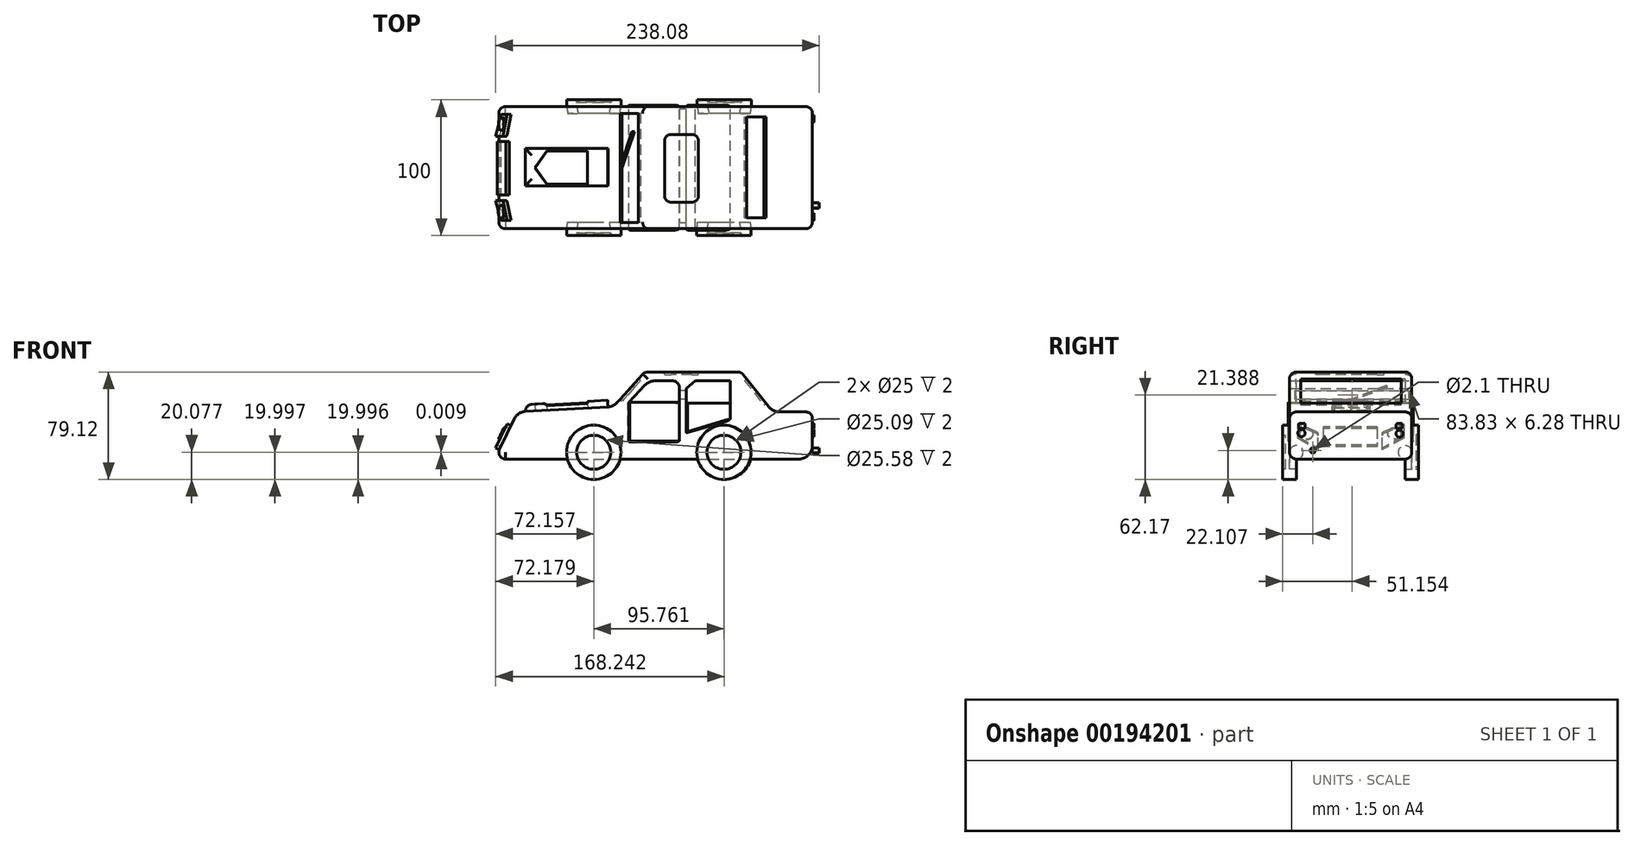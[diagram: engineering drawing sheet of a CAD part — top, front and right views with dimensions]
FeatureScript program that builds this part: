
annotation { "Feature Type Name" : "Feature", "Feature Type Description" : "" }
export const myFeature = defineFeature(function(context is Context, id is Id, definition is map)
    precondition{}
    {
        {
            var Q0;
            Q0=qCreatedBy(makeId("Front.planeOp"),FACE);
            var sketch = newSketch(context, id + "F0", { "sketchPlane" : qUnion([Q0])});
            skLineSegment(sketch, "E0.right", {"start": v(123.47, 0) * mm, "end": v(123.47, -24.73) * mm});
            skLineSegment(sketch, "E1", {"start": v(-110.25, -34.75) * mm, "end": v(-96.18, -5.34) * mm});
            skLineSegment(sketch, "E2", {"start": v(-87.7, 0.33) * mm, "end": v(-26.96, 3.68) * mm});
            skLineSegment(sketch, "E3", {"start": v(-20.07, 6.99) * mm, "end": v(0, 29.38) * mm});
            skLineSegment(sketch, "E4", {"start": v(0, 29.38) * mm, "end": v(70.99, 29.38) * mm});
            skLineSegment(sketch, "E5", {"start": v(70.99, 29.38) * mm, "end": v(91.24, 3.8) * mm});
            skLineSegment(sketch, "E6", {"start": v(99.08, 0) * mm, "end": v(123.47, 0) * mm});
            skLineSegment(sketch, "E7", {"start": v(-110.25, -34.75) * mm, "end": v(-48.86, -34.74) * mm});
            skLineSegment(sketch, "E8.trimOffspring", {"start": v(-8.86, -34.74) * mm, "end": v(46.53, -34.73) * mm});
            skLineSegment(sketch, "E9.trimOffspring", {"start": v(86.53, -34.73) * mm, "end": v(113.47, -34.73) * mm});
            skPoint(sketch, "E10.visualSharp", {"position": v(-22.83, 3.9) * mm});
            skArc(sketch, "E10.filletArc", {"start": v(-26.96, 3.68) * mm, "mid": v(-23.19, 4.65) * mm, "end": v(-20.07, 6.99) * mm});
            skPoint(sketch, "E11.visualSharp", {"position": v(94.24, 0) * mm});
            skArc(sketch, "E11.filletArc", {"start": v(91.24, 3.8) * mm, "mid": v(94.72, 1) * mm, "end": v(99.08, 0) * mm});
            skPoint(sketch, "E12.visualSharp", {"position": v(-93.62, 0) * mm});
            skArc(sketch, "E12.filletArc", {"start": v(-87.7, 0.33) * mm, "mid": v(-92.72, -1.35) * mm, "end": v(-96.18, -5.34) * mm});
            skPoint(sketch, "E13.visualSharp", {"position": v(123.47, -34.73) * mm});
            skArc(sketch, "E13.filletArc", {"start": v(113.47, -34.73) * mm, "mid": v(120.54, -31.8) * mm, "end": v(123.47, -24.73) * mm});
            skLineSegment(sketch, "E14", {"start": v(-11.64, 6.99) * mm, "end": v(0.27, 19.72) * mm});
            skLineSegment(sketch, "E15", {"start": v(7.57, 22.88) * mm, "end": v(20.47, 22.88) * mm});
            skLineSegment(sketch, "E16", {"start": v(25.47, 17.88) * mm, "end": v(25.47, 6.99) * mm});
            skLineSegment(sketch, "E17", {"start": v(25.47, 6.99) * mm, "end": v(-11.64, 6.99) * mm});
            skPoint(sketch, "E18.visualSharp", {"position": v(3.24, 22.88) * mm});
            skArc(sketch, "E18.filletArc", {"start": v(7.57, 22.88) * mm, "mid": v(3.6, 22.06) * mm, "end": v(0.27, 19.72) * mm});
            skPoint(sketch, "E19.visualSharp", {"position": v(25.47, 22.88) * mm});
            skArc(sketch, "E19.filletArc", {"start": v(25.47, 17.88) * mm, "mid": v(24, 21.42) * mm, "end": v(20.47, 22.88) * mm});
            skLineSegment(sketch, "E20", {"start": v(30.75, 17.27) * mm, "end": v(30.75, 6.6) * mm});
            skLineSegment(sketch, "E21", {"start": v(30.75, 6.6) * mm, "end": v(63.04, 6.6) * mm});
            skLineSegment(sketch, "E22", {"start": v(63.04, 6.6) * mm, "end": v(63.04, 22.88) * mm});
            skLineSegment(sketch, "E23", {"start": v(63.04, 22.88) * mm, "end": v(37.2, 22.88) * mm});
            skLineSegment(sketch, "E24", {"start": v(37.2, 22.88) * mm, "end": v(30.75, 17.27) * mm});
            skLineSegment(sketch, "E25", {"start": v(-48.86, -34.74) * mm, "end": v(-8.86, -34.74) * mm});
            skLineSegment(sketch, "E26", {"start": v(46.53, -34.73) * mm, "end": v(86.53, -34.73) * mm});
            skSolve(sketch);
        }
        {
            var Q0;
            Q0=makeQuery(id+"F0.imprint","IMPRINT",FACE,{"disambiguationData":[TD([[makeQuery(id+"F0.imprint","IMPRINT",EDGE,{"derivedFrom":sQuery(id+"F0.wireOp",EDGE,"E1")}),-1.0]])]});
            extrude(context, id + "F1", {"entities" : qUnion([Q0]), "endBound" : BoundingType.SYMMETRIC, "depth" : 90 * mm});
        }
        {
            var Q0;
            Q0=makeQuery(id+"F1.opExtrude","CAP_EDGE",EDGE,{"disambiguationData":[OSD([sQuery(id+"F0.wireOp",EDGE,"E8.trimOffspring")])],"isStart":false});
            var Q1;
            Q1=makeQuery(id+"F1.opExtrude","CAP_EDGE",EDGE,{"disambiguationData":[OSD([sQuery(id+"F0.wireOp",EDGE,"E9.trimOffspring")])],"isStart":false});
            var Q2;
            Q2=makeQuery(id+"F1.opExtrude","CAP_EDGE",EDGE,{"disambiguationData":[OSD([sQuery(id+"F0.wireOp",EDGE,"E7")])],"isStart":false});
            var Q3;
            Q3=makeQuery(id+"F1.opExtrude","CAP_EDGE",EDGE,{"disambiguationData":[OSD([sQuery(id+"F0.wireOp",EDGE,"E7")])],"isStart":true});
            var Q4;
            Q4=makeQuery(id+"F1.opExtrude","CAP_EDGE",EDGE,{"disambiguationData":[OSD([sQuery(id+"F0.wireOp",EDGE,"E8.trimOffspring")])],"isStart":true});
            var Q5;
            Q5=makeQuery(id+"F1.opExtrude","CAP_EDGE",EDGE,{"disambiguationData":[OSD([sQuery(id+"F0.wireOp",EDGE,"E9.trimOffspring")])],"isStart":true});
            fillet(context, id + "F2", {"entities" : qUnion([Q0, Q1, Q2, Q3, Q4, Q5]), "radius" : 5 * mm, "tangentPropagation" : true, "allowEdgeOverflow" : false});
        }
        {
            var Q0;
            Q0=makeQuery(id+"F1.opExtrude","CAP_EDGE",EDGE,{"disambiguationData":[OSD([sQuery(id+"F0.wireOp",EDGE,"E5")])],"isStart":false});
            var Q1;
            Q1=makeQuery(id+"F1.opExtrude","CAP_EDGE",EDGE,{"disambiguationData":[OSD([sQuery(id+"F0.wireOp",EDGE,"E4")])],"isStart":false});
            var Q2;
            Q2=makeQuery(id+"F1.opExtrude","SWEPT_EDGE",EDGE,{"disambiguationData":[OSD([sQuery(id+"F0.wireOp",EDGE,"E4"),sQuery(id+"F0.wireOp",EDGE,"E5")])]});
            var Q3;
            Q3=makeQuery(id+"F1.opExtrude","CAP_EDGE",EDGE,{"disambiguationData":[OSD([sQuery(id+"F0.wireOp",EDGE,"E4")])],"isStart":true});
            var Q4;
            Q4=makeQuery(id+"F1.opExtrude","SWEPT_EDGE",EDGE,{"disambiguationData":[OSD([sQuery(id+"F0.wireOp",EDGE,"E3"),sQuery(id+"F0.wireOp",EDGE,"E4")])]});
            fillet(context, id + "F3", {"entities" : qUnion([Q0, Q1, Q2, Q3, Q4]), "radius" : 5 * mm, "tangentPropagation" : true, "allowEdgeOverflow" : false});
        }
        {
            var Q0;
            Q0=makeQuery(id+"F1.opExtrude","SWEPT_FACE",FACE,{"disambiguationData":[OSD([sQuery(id+"F0.wireOp",EDGE,"E1")])]});
            var sketch = newSketch(context, id + "F4", { "sketchPlane" : qUnion([Q0])});
            skLineSegment(sketch, "E27", {"start": v(-39.13, -51.46) * mm, "end": v(-39.13, -60.89) * mm});
            skLineSegment(sketch, "E28", {"start": v(-38.12, -62.62) * mm, "end": v(-23.15, -71.18) * mm});
            skLineSegment(sketch, "E29", {"start": v(-23.15, -71.18) * mm, "end": v(-23.15, -59.81) * mm});
            skLineSegment(sketch, "E30", {"start": v(-24.34, -57.98) * mm, "end": v(-39.13, -51.46) * mm});
            skLineSegment(sketch, "E31", {"start": v(38.83, -51.46) * mm, "end": v(38.83, -60.94) * mm});
            skLineSegment(sketch, "E32", {"start": v(37.89, -62.63) * mm, "end": v(24.19, -71.18) * mm});
            skLineSegment(sketch, "E33", {"start": v(24.19, -71.18) * mm, "end": v(24.19, -59.76) * mm});
            skLineSegment(sketch, "E34", {"start": v(25.32, -57.96) * mm, "end": v(38.83, -51.46) * mm});
            skPoint(sketch, "E35.visualSharp", {"position": v(-23.15, -58.5) * mm});
            skArc(sketch, "E35.filletArc", {"start": v(-23.15, -59.81) * mm, "mid": v(-23.47, -58.72) * mm, "end": v(-24.34, -57.98) * mm});
            skPoint(sketch, "E36.visualSharp", {"position": v(-39.13, -62.05) * mm});
            skArc(sketch, "E36.filletArc", {"start": v(-39.13, -60.89) * mm, "mid": v(-38.86, -61.9) * mm, "end": v(-38.12, -62.62) * mm});
            skPoint(sketch, "E37.visualSharp", {"position": v(24.19, -58.5) * mm});
            skArc(sketch, "E37.filletArc", {"start": v(25.32, -57.96) * mm, "mid": v(24.5, -58.7) * mm, "end": v(24.19, -59.76) * mm});
            skPoint(sketch, "E38.visualSharp", {"position": v(38.83, -62.05) * mm});
            skArc(sketch, "E38.filletArc", {"start": v(37.89, -62.63) * mm, "mid": v(38.58, -61.9) * mm, "end": v(38.83, -60.94) * mm});
            skCircle(sketch, "E39", {"center": v(-32.1, -59.81) * mm, "radius": 4.75 * mm});
            skCircle(sketch, "E40", {"center": v(32.5, -59.99) * mm, "radius": 4.75 * mm});
            skPoint(sketch, "E41.oppositeSnap0", {"position": v(40, -67.86) * mm});
            skLineSegment(sketch, "E41.bottom", {"start": v(-39.86, -48.02) * mm, "end": v(40, -48.02) * mm});
            skLineSegment(sketch, "E41.top", {"start": v(-39.86, -71.3) * mm, "end": v(40, -71.3) * mm});
            skLineSegment(sketch, "E41.left", {"start": v(-39.86, -48.02) * mm, "end": v(-39.86, -71.3) * mm});
            skLineSegment(sketch, "E41.right", {"start": v(40, -48.02) * mm, "end": v(40, -71.3) * mm});
            skLineSegment(sketch, "E42.bottom", {"start": v(-19.4, -54) * mm, "end": v(20.24, -54) * mm});
            skLineSegment(sketch, "E42.top", {"start": v(-19.4, -68.74) * mm, "end": v(20.24, -68.74) * mm});
            skLineSegment(sketch, "E42.left", {"start": v(-19.4, -54) * mm, "end": v(-19.4, -68.74) * mm});
            skLineSegment(sketch, "E42.right", {"start": v(20.24, -54) * mm, "end": v(20.24, -68.74) * mm});
            skSolve(sketch);
        }
        {
            var Q0;
            Q0=makeQuery(id+"F4.imprint","IMPRINT",FACE,{"disambiguationData":[TD([[makeQuery(id+"F4.imprint","IMPRINT",EDGE,{"derivedFrom":sQuery(id+"F4.wireOp",EDGE,"E27")}),-1.0]])]});
            extrude(context, id + "F5", {"entities" : qUnion([Q0]), "operationType" : NewBodyOperationType.REMOVE, "depth" : 2 * mm});
        }
        {
            var Q0;
            Q0=makeQuery(id+"F1.opExtrude","SWEPT_FACE",FACE,{"disambiguationData":[OSD([sQuery(id+"F0.wireOp",EDGE,"E3")])]});
            var sketch = newSketch(context, id + "F6", { "sketchPlane" : qUnion([Q0])});
            skLineSegment(sketch, "E43.bottom", {"start": v(-40, 15.17) * mm, "end": v(40.3, 15.17) * mm});
            skLineSegment(sketch, "E43.top", {"start": v(-40, -5.22) * mm, "end": v(40.3, -5.22) * mm});
            skLineSegment(sketch, "E43.left", {"start": v(-40, 15.17) * mm, "end": v(-40, -5.22) * mm});
            skLineSegment(sketch, "E43.right", {"start": v(40.3, 15.17) * mm, "end": v(40.3, -5.22) * mm});
            skLineSegment(sketch, "E44", {"start": v(-26.5, 8.65) * mm, "end": v(0, -5.22) * mm});
            skLineSegment(sketch, "E45", {"start": v(-26.64, 7.88) * mm, "end": v(-0.65, -4.88) * mm});
            skLineSegment(sketch, "E46", {"start": v(-26.5, 8.65) * mm, "end": v(-26.64, 7.88) * mm});
            skSolve(sketch);
        }
        {
            var Q0;
            Q0=makeQuery(id+"F6.imprint","IMPRINT",FACE,{"disambiguationData":[TD([[makeQuery(id+"F6.imprint","IMPRINT",EDGE,{"derivedFrom":sQuery(id+"F6.wireOp",EDGE,"E43.bottom")}),-1.0]])]});
            extrude(context, id + "F7", {"entities" : qUnion([Q0]), "operationType" : NewBodyOperationType.REMOVE, "oppositeDirection" : true, "depth" : 2 * mm});
        }
        {
            var Q0;
            Q0=makeQuery(id+"F1.opExtrude","SWEPT_FACE",FACE,{"disambiguationData":[OSD([sQuery(id+"F0.wireOp",EDGE,"E5")])]});
            var sketch = newSketch(context, id + "F8", { "sketchPlane" : qUnion([Q0])});
            skLineSegment(sketch, "E47.bottom", {"start": v(-36.85, -27.57) * mm, "end": v(37.38, -27.57) * mm});
            skLineSegment(sketch, "E47.top", {"start": v(-36.85, -50.4) * mm, "end": v(37.38, -50.4) * mm});
            skLineSegment(sketch, "E47.left", {"start": v(-36.85, -27.57) * mm, "end": v(-36.85, -50.4) * mm});
            skLineSegment(sketch, "E47.right", {"start": v(37.38, -27.57) * mm, "end": v(37.38, -50.4) * mm});
            skSolve(sketch);
        }
        {
            var Q0;
            Q0=makeQuery(id+"F8.imprint","IMPRINT",FACE,{"disambiguationData":[TD([[makeQuery(id+"F8.imprint","IMPRINT",EDGE,{"derivedFrom":sQuery(id+"F8.wireOp",EDGE,"E47.bottom")}),-1.0]])]});
            extrude(context, id + "F9", {"entities" : qUnion([Q0]), "operationType" : NewBodyOperationType.REMOVE, "oppositeDirection" : true, "depth" : 2 * mm});
        }
        {
            var Q0;
            Q0=makeQuery(id+"F1.opExtrude","SWEPT_FACE",FACE,{"disambiguationData":[OSD([sQuery(id+"F0.wireOp",EDGE,"E0.right")])]});
            var sketch = newSketch(context, id + "F10", { "sketchPlane" : qUnion([Q0])});
            skLineSegment(sketch, "E48.bottom", {"start": v(-37.41, -8.5) * mm, "end": v(-33.54, -8.5) * mm});
            skLineSegment(sketch, "E48.top", {"start": v(-38.45, -12.4) * mm, "end": v(-34.58, -12.4) * mm});
            skLineSegment(sketch, "E48.left", {"start": v(-38.45, -9.54) * mm, "end": v(-38.45, -12.4) * mm});
            skLineSegment(sketch, "E48.right", {"start": v(-33.54, -8.5) * mm, "end": v(-33.54, -11.36) * mm});
            skLineSegment(sketch, "E49.bottom", {"start": v(34.53, -8.5) * mm, "end": v(38.02, -8.5) * mm});
            skLineSegment(sketch, "E49.top", {"start": v(33.49, -12.4) * mm, "end": v(36.98, -12.4) * mm});
            skLineSegment(sketch, "E49.left", {"start": v(33.49, -9.55) * mm, "end": v(33.49, -12.4) * mm});
            skLineSegment(sketch, "E49.right", {"start": v(38.02, -8.5) * mm, "end": v(38.02, -11.36) * mm});
            skCircle(sketch, "E50", {"center": v(-36.21, -15.58) * mm, "radius": 2.68 * mm});
            skCircle(sketch, "E51", {"center": v(35.98, -16.04) * mm, "radius": 2.6 * mm});
            skPoint(sketch, "E52.visualSharp", {"position": v(-38.45, -8.5) * mm});
            skArc(sketch, "E52.filletArc", {"start": v(-37.41, -8.5) * mm, "mid": v(-38.15, -8.81) * mm, "end": v(-38.45, -9.54) * mm});
            skPoint(sketch, "E53.visualSharp", {"position": v(-33.54, -12.4) * mm});
            skArc(sketch, "E53.filletArc", {"start": v(-34.58, -12.4) * mm, "mid": v(-33.84, -12.1) * mm, "end": v(-33.54, -11.36) * mm});
            skPoint(sketch, "E54.visualSharp", {"position": v(33.49, -8.5) * mm});
            skArc(sketch, "E54.filletArc", {"start": v(34.53, -8.5) * mm, "mid": v(33.8, -8.81) * mm, "end": v(33.49, -9.55) * mm});
            skPoint(sketch, "E55.visualSharp", {"position": v(38.02, -12.4) * mm});
            skArc(sketch, "E55.filletArc", {"start": v(36.98, -12.4) * mm, "mid": v(37.71, -12.1) * mm, "end": v(38.02, -11.36) * mm});
            skSolve(sketch);
        }
        {
            var Q0;
            Q0=makeQuery(id+"F10.imprint","IMPRINT",FACE,{"disambiguationData":[TD([[makeQuery(id+"F10.imprint","IMPRINT",EDGE,{"derivedFrom":sQuery(id+"F10.wireOp",EDGE,"E48.bottom")}),-1.0]])]});
            var Q1;
            Q1=makeQuery(id+"F10.imprint","IMPRINT",FACE,{"disambiguationData":[TD([[makeQuery(id+"F10.imprint","IMPRINT",EDGE,{"derivedFrom":sQuery(id+"F10.wireOp",EDGE,"E49.bottom")}),-1.0]])]});
            var Q2;
            Q2=makeQuery(id+"F10.imprint","IMPRINT",FACE,{"disambiguationData":[TD([[makeQuery(id+"F10.imprint","IMPRINT",EDGE,{"derivedFrom":sQuery(id+"F10.wireOp",EDGE,"E50")}),1.0]])]});
            var Q3;
            Q3=makeQuery(id+"F10.imprint","IMPRINT",FACE,{"disambiguationData":[TD([[makeQuery(id+"F10.imprint","IMPRINT",EDGE,{"derivedFrom":sQuery(id+"F10.wireOp",EDGE,"E51")}),1.0]])]});
            extrude(context, id + "F11", {"entities" : qUnion([Q0, Q1, Q2, Q3]), "operationType" : NewBodyOperationType.ADD, "depth" : 1 * mm});
        }
        {
            var Q0;
            Q0=makeQuery(id+"F1.opExtrude","CAP_FACE",FACE,{"disambiguationData":[OSD([sQuery(id+"F0.wireOp",EDGE,"E1"),sQuery(id+"F0.wireOp",EDGE,"E2"),sQuery(id+"F0.wireOp",EDGE,"E3"),sQuery(id+"F0.wireOp",EDGE,"E4"),sQuery(id+"F0.wireOp",EDGE,"E5"),sQuery(id+"F0.wireOp",EDGE,"E6"),sQuery(id+"F0.wireOp",EDGE,"E0.right"),sQuery(id+"F0.wireOp",EDGE,"E7"),sQuery(id+"F0.wireOp",EDGE,"E8.trimOffspring"),sQuery(id+"F0.wireOp",EDGE,"E9.trimOffspring"),sQuery(id+"F0.wireOp",EDGE,"E10.filletArc"),sQuery(id+"F0.wireOp",EDGE,"E11.filletArc"),sQuery(id+"F0.wireOp",EDGE,"E12.filletArc"),sQuery(id+"F0.wireOp",EDGE,"E13.filletArc"),sQuery(id+"F0.wireOp",EDGE,"E14"),sQuery(id+"F0.wireOp",EDGE,"E15"),sQuery(id+"F0.wireOp",EDGE,"E16"),sQuery(id+"F0.wireOp",EDGE,"E17"),sQuery(id+"F0.wireOp",EDGE,"E18.filletArc"),sQuery(id+"F0.wireOp",EDGE,"E19.filletArc"),sQuery(id+"F0.wireOp",EDGE,"E20"),sQuery(id+"F0.wireOp",EDGE,"E21"),sQuery(id+"F0.wireOp",EDGE,"E22"),sQuery(id+"F0.wireOp",EDGE,"E23"),sQuery(id+"F0.wireOp",EDGE,"E24"),sQuery(id+"F0.wireOp",EDGE,"E25"),sQuery(id+"F0.wireOp",EDGE,"E26")])],"isStart":false});
            var sketch = newSketch(context, id + "F12", { "sketchPlane" : qUnion([Q0])});
            skCircle(sketch, "E56", {"center": v(-37.45, -29.74) * mm, "radius": 20 * mm});
            skCircle(sketch, "E57", {"center": v(58.3, -29.73) * mm, "radius": 20 * mm});
            skCircle(sketch, "E58", {"center": v(-37.45, -29.74) * mm, "radius": 12.5 * mm});
            skCircle(sketch, "E59", {"center": v(58.3, -29.73) * mm, "radius": 12.5 * mm});
            skLineSegment(sketch, "E60", {"start": v(25.47, 3.14) * mm, "end": v(25.47, -22.14) * mm});
            skPoint(sketch, "E60.startSnap0", {"position": v(25.47, 12.43) * mm});
            skLineSegment(sketch, "E61", {"start": v(25.47, -22.14) * mm, "end": v(-11.64, -22.14) * mm});
            skLineSegment(sketch, "E62", {"start": v(-11.64, -22.14) * mm, "end": v(-11.64, 6.99) * mm});
            skLineSegment(sketch, "E63", {"start": v(-11.64, 6.99) * mm, "end": v(25.47, 6.99) * mm});
            skLineSegment(sketch, "E64", {"start": v(25.47, 6.99) * mm, "end": v(25.47, 3.14) * mm});
            skLineSegment(sketch, "E65", {"start": v(30.75, 3.14) * mm, "end": v(30.75, -15.58) * mm});
            skLineSegment(sketch, "E66", {"start": v(30.75, -15.58) * mm, "end": v(62.88, -5.93) * mm});
            skLineSegment(sketch, "E67", {"start": v(62.88, -5.93) * mm, "end": v(63.04, 6.6) * mm});
            skLineSegment(sketch, "E68", {"start": v(63.04, 6.6) * mm, "end": v(30.75, 6.6) * mm});
            skLineSegment(sketch, "E69", {"start": v(30.75, 6.6) * mm, "end": v(30.75, 3.14) * mm});
            skSolve(sketch);
        }
        {
            var Q0;
            {var subQ0=sQuery(id+"F12.wireOp",EDGE,"E56");var subQ1=sQuery(id+"F0.wireOp",EDGE,"E26");var subQ2=sQuery(id+"F0.wireOp",EDGE,"E25");var subQ3=sQuery(id+"F0.wireOp",EDGE,"E9.trimOffspring");var subQ4=sQuery(id+"F0.wireOp",EDGE,"E8.trimOffspring");var subQ5=sQuery(id+"F0.wireOp",EDGE,"E7");var subQ6=makeQuery(id+"F2.opFillet","BLEND_EDGE",EDGE,{"blendedFrom":[makeQuery(id+"F1.opExtrude","CAP_EDGE",EDGE,{"disambiguationData":[OSD([subQ5,subQ4,subQ3,subQ2,subQ1])],"isStart":false}),makeQuery(id+"F1.opExtrude","CAP_FACE",FACE,{"disambiguationData":[OSD([sQuery(id+"F0.wireOp",EDGE,"E1"),sQuery(id+"F0.wireOp",EDGE,"E2"),sQuery(id+"F0.wireOp",EDGE,"E3"),sQuery(id+"F0.wireOp",EDGE,"E4"),sQuery(id+"F0.wireOp",EDGE,"E5"),sQuery(id+"F0.wireOp",EDGE,"E6"),sQuery(id+"F0.wireOp",EDGE,"E0.right"),subQ5,subQ4,subQ3,sQuery(id+"F0.wireOp",EDGE,"E10.filletArc"),sQuery(id+"F0.wireOp",EDGE,"E11.filletArc"),sQuery(id+"F0.wireOp",EDGE,"E12.filletArc"),sQuery(id+"F0.wireOp",EDGE,"E13.filletArc"),sQuery(id+"F0.wireOp",EDGE,"E14"),sQuery(id+"F0.wireOp",EDGE,"E15"),sQuery(id+"F0.wireOp",EDGE,"E16"),sQuery(id+"F0.wireOp",EDGE,"E17"),sQuery(id+"F0.wireOp",EDGE,"E18.filletArc"),sQuery(id+"F0.wireOp",EDGE,"E19.filletArc"),sQuery(id+"F0.wireOp",EDGE,"E20"),sQuery(id+"F0.wireOp",EDGE,"E21"),sQuery(id+"F0.wireOp",EDGE,"E22"),sQuery(id+"F0.wireOp",EDGE,"E23"),sQuery(id+"F0.wireOp",EDGE,"E24"),subQ2,subQ1])],"isStart":false})],"blendedInto":[makeQuery(id+"F1.opExtrude","CAP_FACE",FACE,{"disambiguationData":[OSD([sQuery(id+"F0.wireOp",EDGE,"E1"),sQuery(id+"F0.wireOp",EDGE,"E2"),sQuery(id+"F0.wireOp",EDGE,"E3"),sQuery(id+"F0.wireOp",EDGE,"E4"),sQuery(id+"F0.wireOp",EDGE,"E5"),sQuery(id+"F0.wireOp",EDGE,"E6"),sQuery(id+"F0.wireOp",EDGE,"E0.right"),subQ5,subQ4,subQ3,sQuery(id+"F0.wireOp",EDGE,"E10.filletArc"),sQuery(id+"F0.wireOp",EDGE,"E11.filletArc"),sQuery(id+"F0.wireOp",EDGE,"E12.filletArc"),sQuery(id+"F0.wireOp",EDGE,"E13.filletArc"),sQuery(id+"F0.wireOp",EDGE,"E14"),sQuery(id+"F0.wireOp",EDGE,"E15"),sQuery(id+"F0.wireOp",EDGE,"E16"),sQuery(id+"F0.wireOp",EDGE,"E17"),sQuery(id+"F0.wireOp",EDGE,"E18.filletArc"),sQuery(id+"F0.wireOp",EDGE,"E19.filletArc"),sQuery(id+"F0.wireOp",EDGE,"E20"),sQuery(id+"F0.wireOp",EDGE,"E21"),sQuery(id+"F0.wireOp",EDGE,"E22"),sQuery(id+"F0.wireOp",EDGE,"E23"),sQuery(id+"F0.wireOp",EDGE,"E24"),subQ2,subQ1])],"isStart":false})]});var subQ7=makeQuery(id+"F12.imprint","INTERSECT",VERTEX,{"disambiguationData":[OD(0.0)],"derivedFrom":[subQ6,subQ0]});Q0=makeQuery(id+"F12.imprint","IMPRINT",FACE,{"disambiguationData":[TD([[makeQuery(id+"F12.imprint","IMPRINT",EDGE,{"disambiguationData":[TD([[subQ7,-1.0]])],"derivedFrom":subQ0}),1.0]])]});}
            var Q1;
            {var subQ0=sQuery(id+"F12.wireOp",EDGE,"E57");var subQ1=sQuery(id+"F0.wireOp",EDGE,"E26");var subQ2=sQuery(id+"F0.wireOp",EDGE,"E25");var subQ3=sQuery(id+"F0.wireOp",EDGE,"E9.trimOffspring");var subQ4=sQuery(id+"F0.wireOp",EDGE,"E8.trimOffspring");var subQ5=sQuery(id+"F0.wireOp",EDGE,"E7");var subQ6=makeQuery(id+"F2.opFillet","BLEND_EDGE",EDGE,{"blendedFrom":[makeQuery(id+"F1.opExtrude","CAP_EDGE",EDGE,{"disambiguationData":[OSD([subQ5,subQ4,subQ3,subQ2,subQ1])],"isStart":false}),makeQuery(id+"F1.opExtrude","CAP_FACE",FACE,{"disambiguationData":[OSD([sQuery(id+"F0.wireOp",EDGE,"E1"),sQuery(id+"F0.wireOp",EDGE,"E2"),sQuery(id+"F0.wireOp",EDGE,"E3"),sQuery(id+"F0.wireOp",EDGE,"E4"),sQuery(id+"F0.wireOp",EDGE,"E5"),sQuery(id+"F0.wireOp",EDGE,"E6"),sQuery(id+"F0.wireOp",EDGE,"E0.right"),subQ5,subQ4,subQ3,sQuery(id+"F0.wireOp",EDGE,"E10.filletArc"),sQuery(id+"F0.wireOp",EDGE,"E11.filletArc"),sQuery(id+"F0.wireOp",EDGE,"E12.filletArc"),sQuery(id+"F0.wireOp",EDGE,"E13.filletArc"),sQuery(id+"F0.wireOp",EDGE,"E14"),sQuery(id+"F0.wireOp",EDGE,"E15"),sQuery(id+"F0.wireOp",EDGE,"E16"),sQuery(id+"F0.wireOp",EDGE,"E17"),sQuery(id+"F0.wireOp",EDGE,"E18.filletArc"),sQuery(id+"F0.wireOp",EDGE,"E19.filletArc"),sQuery(id+"F0.wireOp",EDGE,"E20"),sQuery(id+"F0.wireOp",EDGE,"E21"),sQuery(id+"F0.wireOp",EDGE,"E22"),sQuery(id+"F0.wireOp",EDGE,"E23"),sQuery(id+"F0.wireOp",EDGE,"E24"),subQ2,subQ1])],"isStart":false})],"blendedInto":[makeQuery(id+"F1.opExtrude","CAP_FACE",FACE,{"disambiguationData":[OSD([sQuery(id+"F0.wireOp",EDGE,"E1"),sQuery(id+"F0.wireOp",EDGE,"E2"),sQuery(id+"F0.wireOp",EDGE,"E3"),sQuery(id+"F0.wireOp",EDGE,"E4"),sQuery(id+"F0.wireOp",EDGE,"E5"),sQuery(id+"F0.wireOp",EDGE,"E6"),sQuery(id+"F0.wireOp",EDGE,"E0.right"),subQ5,subQ4,subQ3,sQuery(id+"F0.wireOp",EDGE,"E10.filletArc"),sQuery(id+"F0.wireOp",EDGE,"E11.filletArc"),sQuery(id+"F0.wireOp",EDGE,"E12.filletArc"),sQuery(id+"F0.wireOp",EDGE,"E13.filletArc"),sQuery(id+"F0.wireOp",EDGE,"E14"),sQuery(id+"F0.wireOp",EDGE,"E15"),sQuery(id+"F0.wireOp",EDGE,"E16"),sQuery(id+"F0.wireOp",EDGE,"E17"),sQuery(id+"F0.wireOp",EDGE,"E18.filletArc"),sQuery(id+"F0.wireOp",EDGE,"E19.filletArc"),sQuery(id+"F0.wireOp",EDGE,"E20"),sQuery(id+"F0.wireOp",EDGE,"E21"),sQuery(id+"F0.wireOp",EDGE,"E22"),sQuery(id+"F0.wireOp",EDGE,"E23"),sQuery(id+"F0.wireOp",EDGE,"E24"),subQ2,subQ1])],"isStart":false})]});var subQ7=makeQuery(id+"F12.imprint","INTERSECT",VERTEX,{"disambiguationData":[OD(0.0)],"derivedFrom":[subQ6,subQ0]});Q1=makeQuery(id+"F12.imprint","IMPRINT",FACE,{"disambiguationData":[TD([[makeQuery(id+"F12.imprint","IMPRINT",EDGE,{"disambiguationData":[TD([[subQ7,1.0]])],"derivedFrom":subQ0}),1.0]])]});}
            var Q2;
            {var subQ0=sQuery(id+"F12.wireOp",EDGE,"E56");var subQ1=sQuery(id+"F0.wireOp",EDGE,"E26");var subQ2=sQuery(id+"F0.wireOp",EDGE,"E25");var subQ3=sQuery(id+"F0.wireOp",EDGE,"E9.trimOffspring");var subQ4=sQuery(id+"F0.wireOp",EDGE,"E8.trimOffspring");var subQ5=sQuery(id+"F0.wireOp",EDGE,"E7");var subQ6=makeQuery(id+"F2.opFillet","BLEND_EDGE",EDGE,{"blendedFrom":[makeQuery(id+"F1.opExtrude","CAP_EDGE",EDGE,{"disambiguationData":[OSD([subQ5,subQ4,subQ3,subQ2,subQ1])],"isStart":false}),makeQuery(id+"F1.opExtrude","CAP_FACE",FACE,{"disambiguationData":[OSD([sQuery(id+"F0.wireOp",EDGE,"E1"),sQuery(id+"F0.wireOp",EDGE,"E2"),sQuery(id+"F0.wireOp",EDGE,"E3"),sQuery(id+"F0.wireOp",EDGE,"E4"),sQuery(id+"F0.wireOp",EDGE,"E5"),sQuery(id+"F0.wireOp",EDGE,"E6"),sQuery(id+"F0.wireOp",EDGE,"E0.right"),subQ5,subQ4,subQ3,sQuery(id+"F0.wireOp",EDGE,"E10.filletArc"),sQuery(id+"F0.wireOp",EDGE,"E11.filletArc"),sQuery(id+"F0.wireOp",EDGE,"E12.filletArc"),sQuery(id+"F0.wireOp",EDGE,"E13.filletArc"),sQuery(id+"F0.wireOp",EDGE,"E14"),sQuery(id+"F0.wireOp",EDGE,"E15"),sQuery(id+"F0.wireOp",EDGE,"E16"),sQuery(id+"F0.wireOp",EDGE,"E17"),sQuery(id+"F0.wireOp",EDGE,"E18.filletArc"),sQuery(id+"F0.wireOp",EDGE,"E19.filletArc"),sQuery(id+"F0.wireOp",EDGE,"E20"),sQuery(id+"F0.wireOp",EDGE,"E21"),sQuery(id+"F0.wireOp",EDGE,"E22"),sQuery(id+"F0.wireOp",EDGE,"E23"),sQuery(id+"F0.wireOp",EDGE,"E24"),subQ2,subQ1])],"isStart":false})],"blendedInto":[makeQuery(id+"F1.opExtrude","CAP_FACE",FACE,{"disambiguationData":[OSD([sQuery(id+"F0.wireOp",EDGE,"E1"),sQuery(id+"F0.wireOp",EDGE,"E2"),sQuery(id+"F0.wireOp",EDGE,"E3"),sQuery(id+"F0.wireOp",EDGE,"E4"),sQuery(id+"F0.wireOp",EDGE,"E5"),sQuery(id+"F0.wireOp",EDGE,"E6"),sQuery(id+"F0.wireOp",EDGE,"E0.right"),subQ5,subQ4,subQ3,sQuery(id+"F0.wireOp",EDGE,"E10.filletArc"),sQuery(id+"F0.wireOp",EDGE,"E11.filletArc"),sQuery(id+"F0.wireOp",EDGE,"E12.filletArc"),sQuery(id+"F0.wireOp",EDGE,"E13.filletArc"),sQuery(id+"F0.wireOp",EDGE,"E14"),sQuery(id+"F0.wireOp",EDGE,"E15"),sQuery(id+"F0.wireOp",EDGE,"E16"),sQuery(id+"F0.wireOp",EDGE,"E17"),sQuery(id+"F0.wireOp",EDGE,"E18.filletArc"),sQuery(id+"F0.wireOp",EDGE,"E19.filletArc"),sQuery(id+"F0.wireOp",EDGE,"E20"),sQuery(id+"F0.wireOp",EDGE,"E21"),sQuery(id+"F0.wireOp",EDGE,"E22"),sQuery(id+"F0.wireOp",EDGE,"E23"),sQuery(id+"F0.wireOp",EDGE,"E24"),subQ2,subQ1])],"isStart":false})]});var subQ7=makeQuery(id+"F12.imprint","INTERSECT",VERTEX,{"disambiguationData":[OD(0.0)],"derivedFrom":[subQ6,subQ0]});Q2=makeQuery(id+"F12.imprint","IMPRINT",FACE,{"disambiguationData":[TD([[makeQuery(id+"F12.imprint","IMPRINT",EDGE,{"disambiguationData":[TD([[subQ7,1.0]])],"derivedFrom":subQ0}),1.0]])]});}
            var Q3;
            {var subQ0=sQuery(id+"F12.wireOp",EDGE,"E57");var subQ1=sQuery(id+"F0.wireOp",EDGE,"E26");var subQ2=sQuery(id+"F0.wireOp",EDGE,"E25");var subQ3=sQuery(id+"F0.wireOp",EDGE,"E9.trimOffspring");var subQ4=sQuery(id+"F0.wireOp",EDGE,"E8.trimOffspring");var subQ5=sQuery(id+"F0.wireOp",EDGE,"E7");var subQ6=makeQuery(id+"F2.opFillet","BLEND_EDGE",EDGE,{"blendedFrom":[makeQuery(id+"F1.opExtrude","CAP_EDGE",EDGE,{"disambiguationData":[OSD([subQ5,subQ4,subQ3,subQ2,subQ1])],"isStart":false}),makeQuery(id+"F1.opExtrude","CAP_FACE",FACE,{"disambiguationData":[OSD([sQuery(id+"F0.wireOp",EDGE,"E1"),sQuery(id+"F0.wireOp",EDGE,"E2"),sQuery(id+"F0.wireOp",EDGE,"E3"),sQuery(id+"F0.wireOp",EDGE,"E4"),sQuery(id+"F0.wireOp",EDGE,"E5"),sQuery(id+"F0.wireOp",EDGE,"E6"),sQuery(id+"F0.wireOp",EDGE,"E0.right"),subQ5,subQ4,subQ3,sQuery(id+"F0.wireOp",EDGE,"E10.filletArc"),sQuery(id+"F0.wireOp",EDGE,"E11.filletArc"),sQuery(id+"F0.wireOp",EDGE,"E12.filletArc"),sQuery(id+"F0.wireOp",EDGE,"E13.filletArc"),sQuery(id+"F0.wireOp",EDGE,"E14"),sQuery(id+"F0.wireOp",EDGE,"E15"),sQuery(id+"F0.wireOp",EDGE,"E16"),sQuery(id+"F0.wireOp",EDGE,"E17"),sQuery(id+"F0.wireOp",EDGE,"E18.filletArc"),sQuery(id+"F0.wireOp",EDGE,"E19.filletArc"),sQuery(id+"F0.wireOp",EDGE,"E20"),sQuery(id+"F0.wireOp",EDGE,"E21"),sQuery(id+"F0.wireOp",EDGE,"E22"),sQuery(id+"F0.wireOp",EDGE,"E23"),sQuery(id+"F0.wireOp",EDGE,"E24"),subQ2,subQ1])],"isStart":false})],"blendedInto":[makeQuery(id+"F1.opExtrude","CAP_FACE",FACE,{"disambiguationData":[OSD([sQuery(id+"F0.wireOp",EDGE,"E1"),sQuery(id+"F0.wireOp",EDGE,"E2"),sQuery(id+"F0.wireOp",EDGE,"E3"),sQuery(id+"F0.wireOp",EDGE,"E4"),sQuery(id+"F0.wireOp",EDGE,"E5"),sQuery(id+"F0.wireOp",EDGE,"E6"),sQuery(id+"F0.wireOp",EDGE,"E0.right"),subQ5,subQ4,subQ3,sQuery(id+"F0.wireOp",EDGE,"E10.filletArc"),sQuery(id+"F0.wireOp",EDGE,"E11.filletArc"),sQuery(id+"F0.wireOp",EDGE,"E12.filletArc"),sQuery(id+"F0.wireOp",EDGE,"E13.filletArc"),sQuery(id+"F0.wireOp",EDGE,"E14"),sQuery(id+"F0.wireOp",EDGE,"E15"),sQuery(id+"F0.wireOp",EDGE,"E16"),sQuery(id+"F0.wireOp",EDGE,"E17"),sQuery(id+"F0.wireOp",EDGE,"E18.filletArc"),sQuery(id+"F0.wireOp",EDGE,"E19.filletArc"),sQuery(id+"F0.wireOp",EDGE,"E20"),sQuery(id+"F0.wireOp",EDGE,"E21"),sQuery(id+"F0.wireOp",EDGE,"E22"),sQuery(id+"F0.wireOp",EDGE,"E23"),sQuery(id+"F0.wireOp",EDGE,"E24"),subQ2,subQ1])],"isStart":false})]});var subQ7=makeQuery(id+"F12.imprint","INTERSECT",VERTEX,{"disambiguationData":[OD(0.0)],"derivedFrom":[subQ6,subQ0]});Q3=makeQuery(id+"F12.imprint","IMPRINT",FACE,{"disambiguationData":[TD([[makeQuery(id+"F12.imprint","IMPRINT",EDGE,{"disambiguationData":[TD([[subQ7,-1.0]])],"derivedFrom":subQ0}),1.0]])]});}
            var Q4;
            Q4=sQuery(id+"F12.wireOp",EDGE,"E56");
            var Q5;
            Q5=sQuery(id+"F12.wireOp",EDGE,"E57");
            extrude(context, id + "F13", {"entities" : qUnion([Q0, Q1, Q2, Q3]), "operationType" : NewBodyOperationType.ADD, "surfaceEntities" : qUnion([Q4, Q5]), "endBound" : BoundingType.SYMMETRIC, "oppositeDirection" : true, "depth" : 10 * mm});
        }
        {
            var Q0;
            Q0=makeQuery(id+"F1.opExtrude","CAP_FACE",FACE,{"disambiguationData":[OSD([sQuery(id+"F0.wireOp",EDGE,"E1"),sQuery(id+"F0.wireOp",EDGE,"E2"),sQuery(id+"F0.wireOp",EDGE,"E3"),sQuery(id+"F0.wireOp",EDGE,"E4"),sQuery(id+"F0.wireOp",EDGE,"E5"),sQuery(id+"F0.wireOp",EDGE,"E6"),sQuery(id+"F0.wireOp",EDGE,"E0.right"),sQuery(id+"F0.wireOp",EDGE,"E7"),sQuery(id+"F0.wireOp",EDGE,"E8.trimOffspring"),sQuery(id+"F0.wireOp",EDGE,"E9.trimOffspring"),sQuery(id+"F0.wireOp",EDGE,"E10.filletArc"),sQuery(id+"F0.wireOp",EDGE,"E11.filletArc"),sQuery(id+"F0.wireOp",EDGE,"E12.filletArc"),sQuery(id+"F0.wireOp",EDGE,"E13.filletArc"),sQuery(id+"F0.wireOp",EDGE,"E14"),sQuery(id+"F0.wireOp",EDGE,"E15"),sQuery(id+"F0.wireOp",EDGE,"E16"),sQuery(id+"F0.wireOp",EDGE,"E17"),sQuery(id+"F0.wireOp",EDGE,"E18.filletArc"),sQuery(id+"F0.wireOp",EDGE,"E19.filletArc"),sQuery(id+"F0.wireOp",EDGE,"E20"),sQuery(id+"F0.wireOp",EDGE,"E21"),sQuery(id+"F0.wireOp",EDGE,"E22"),sQuery(id+"F0.wireOp",EDGE,"E23"),sQuery(id+"F0.wireOp",EDGE,"E24"),sQuery(id+"F0.wireOp",EDGE,"E25"),sQuery(id+"F0.wireOp",EDGE,"E26")])],"isStart":true});
            var sketch = newSketch(context, id + "F14", { "sketchPlane" : qUnion([Q0])});
            skSolve(sketch);
        }
        {
            var Q0;
            {var subQ25=sQuery(id+"F0.wireOp",EDGE,"E2");Q0=makeQuery(id+"F14.imprint","IMPRINT",FACE,{"disambiguationData":[TD([[makeQuery(id+"F14.imprint","IMPRINT",EDGE,{"derivedFrom":makeQuery(id+"F1.opExtrude","CAP_EDGE",EDGE,{"disambiguationData":[OSD([subQ25])],"isStart":true})}),1.0]])]});}
            var sketch = newSketch(context, id + "F15", { "sketchPlane" : qUnion([Q0])});
            skCircle(sketch, "E70", {"center": v(-58.63, -29.74) * mm, "radius": 20 * mm});
            skCircle(sketch, "E71", {"center": v(37.43, -29.66) * mm, "radius": 20 * mm});
            skCircle(sketch, "E72", {"center": v(-58.63, -29.74) * mm, "radius": 12.54 * mm});
            skCircle(sketch, "E73", {"center": v(37.43, -29.66) * mm, "radius": 12.8 * mm});
            skLineSegment(sketch, "E74", {"start": v(-25.51, 6.56) * mm, "end": v(-25.51, -21.73) * mm});
            skLineSegment(sketch, "E75", {"start": v(-25.51, -21.73) * mm, "end": v(12.22, -21.73) * mm});
            skLineSegment(sketch, "E76", {"start": v(12.22, -21.73) * mm, "end": v(12.22, 7.13) * mm});
            skLineSegment(sketch, "E77", {"start": v(12.22, 7.13) * mm, "end": v(-25.51, 6.56) * mm});
            skLineSegment(sketch, "E78", {"start": v(-30.63, 6.56) * mm, "end": v(-30.68, -15.7) * mm});
            skLineSegment(sketch, "E79", {"start": v(-30.68, -15.7) * mm, "end": v(-62.86, -5.73) * mm});
            skLineSegment(sketch, "E80", {"start": v(-62.86, -5.73) * mm, "end": v(-62.86, 6.56) * mm});
            skLineSegment(sketch, "E81", {"start": v(-62.86, 6.56) * mm, "end": v(-30.63, 6.56) * mm});
            skSolve(sketch);
        }
        {
            var Q0;
            {var subQ0=sQuery(id+"F15.wireOp",EDGE,"E70");var subQ1=sQuery(id+"F0.wireOp",EDGE,"E26");var subQ2=sQuery(id+"F0.wireOp",EDGE,"E25");var subQ3=sQuery(id+"F0.wireOp",EDGE,"E9.trimOffspring");var subQ4=sQuery(id+"F0.wireOp",EDGE,"E8.trimOffspring");var subQ5=sQuery(id+"F0.wireOp",EDGE,"E7");var subQ6=makeQuery(id+"F14.imprint","IMPRINT",EDGE,{"derivedFrom":makeQuery(id+"F2.opFillet","BLEND_EDGE",EDGE,{"blendedFrom":[makeQuery(id+"F1.opExtrude","CAP_EDGE",EDGE,{"disambiguationData":[OSD([subQ5,subQ4,subQ3,subQ2,subQ1])],"isStart":true}),makeQuery(id+"F1.opExtrude","CAP_FACE",FACE,{"disambiguationData":[OSD([sQuery(id+"F0.wireOp",EDGE,"E1"),sQuery(id+"F0.wireOp",EDGE,"E2"),sQuery(id+"F0.wireOp",EDGE,"E3"),sQuery(id+"F0.wireOp",EDGE,"E4"),sQuery(id+"F0.wireOp",EDGE,"E5"),sQuery(id+"F0.wireOp",EDGE,"E6"),sQuery(id+"F0.wireOp",EDGE,"E0.right"),subQ5,subQ4,subQ3,sQuery(id+"F0.wireOp",EDGE,"E10.filletArc"),sQuery(id+"F0.wireOp",EDGE,"E11.filletArc"),sQuery(id+"F0.wireOp",EDGE,"E12.filletArc"),sQuery(id+"F0.wireOp",EDGE,"E13.filletArc"),sQuery(id+"F0.wireOp",EDGE,"E14"),sQuery(id+"F0.wireOp",EDGE,"E15"),sQuery(id+"F0.wireOp",EDGE,"E16"),sQuery(id+"F0.wireOp",EDGE,"E17"),sQuery(id+"F0.wireOp",EDGE,"E18.filletArc"),sQuery(id+"F0.wireOp",EDGE,"E19.filletArc"),sQuery(id+"F0.wireOp",EDGE,"E20"),sQuery(id+"F0.wireOp",EDGE,"E21"),sQuery(id+"F0.wireOp",EDGE,"E22"),sQuery(id+"F0.wireOp",EDGE,"E23"),sQuery(id+"F0.wireOp",EDGE,"E24"),subQ2,subQ1])],"isStart":true})],"blendedInto":[makeQuery(id+"F1.opExtrude","CAP_FACE",FACE,{"disambiguationData":[OSD([sQuery(id+"F0.wireOp",EDGE,"E1"),sQuery(id+"F0.wireOp",EDGE,"E2"),sQuery(id+"F0.wireOp",EDGE,"E3"),sQuery(id+"F0.wireOp",EDGE,"E4"),sQuery(id+"F0.wireOp",EDGE,"E5"),sQuery(id+"F0.wireOp",EDGE,"E6"),sQuery(id+"F0.wireOp",EDGE,"E0.right"),subQ5,subQ4,subQ3,sQuery(id+"F0.wireOp",EDGE,"E10.filletArc"),sQuery(id+"F0.wireOp",EDGE,"E11.filletArc"),sQuery(id+"F0.wireOp",EDGE,"E12.filletArc"),sQuery(id+"F0.wireOp",EDGE,"E13.filletArc"),sQuery(id+"F0.wireOp",EDGE,"E14"),sQuery(id+"F0.wireOp",EDGE,"E15"),sQuery(id+"F0.wireOp",EDGE,"E16"),sQuery(id+"F0.wireOp",EDGE,"E17"),sQuery(id+"F0.wireOp",EDGE,"E18.filletArc"),sQuery(id+"F0.wireOp",EDGE,"E19.filletArc"),sQuery(id+"F0.wireOp",EDGE,"E20"),sQuery(id+"F0.wireOp",EDGE,"E21"),sQuery(id+"F0.wireOp",EDGE,"E22"),sQuery(id+"F0.wireOp",EDGE,"E23"),sQuery(id+"F0.wireOp",EDGE,"E24"),subQ2,subQ1])],"isStart":true})]})});var subQ7=makeQuery(id+"F15.imprint","INTERSECT",VERTEX,{"disambiguationData":[OD(0.0)],"derivedFrom":[subQ6,subQ0]});Q0=makeQuery(id+"F15.imprint","IMPRINT",FACE,{"disambiguationData":[TD([[makeQuery(id+"F15.imprint","IMPRINT",EDGE,{"disambiguationData":[TD([[subQ7,-1.0]])],"derivedFrom":subQ0}),1.0]])]});}
            var Q1;
            {var subQ0=sQuery(id+"F15.wireOp",EDGE,"E70");var subQ1=sQuery(id+"F0.wireOp",EDGE,"E26");var subQ2=sQuery(id+"F0.wireOp",EDGE,"E25");var subQ3=sQuery(id+"F0.wireOp",EDGE,"E9.trimOffspring");var subQ4=sQuery(id+"F0.wireOp",EDGE,"E8.trimOffspring");var subQ5=sQuery(id+"F0.wireOp",EDGE,"E7");var subQ6=makeQuery(id+"F14.imprint","IMPRINT",EDGE,{"derivedFrom":makeQuery(id+"F2.opFillet","BLEND_EDGE",EDGE,{"blendedFrom":[makeQuery(id+"F1.opExtrude","CAP_EDGE",EDGE,{"disambiguationData":[OSD([subQ5,subQ4,subQ3,subQ2,subQ1])],"isStart":true}),makeQuery(id+"F1.opExtrude","CAP_FACE",FACE,{"disambiguationData":[OSD([sQuery(id+"F0.wireOp",EDGE,"E1"),sQuery(id+"F0.wireOp",EDGE,"E2"),sQuery(id+"F0.wireOp",EDGE,"E3"),sQuery(id+"F0.wireOp",EDGE,"E4"),sQuery(id+"F0.wireOp",EDGE,"E5"),sQuery(id+"F0.wireOp",EDGE,"E6"),sQuery(id+"F0.wireOp",EDGE,"E0.right"),subQ5,subQ4,subQ3,sQuery(id+"F0.wireOp",EDGE,"E10.filletArc"),sQuery(id+"F0.wireOp",EDGE,"E11.filletArc"),sQuery(id+"F0.wireOp",EDGE,"E12.filletArc"),sQuery(id+"F0.wireOp",EDGE,"E13.filletArc"),sQuery(id+"F0.wireOp",EDGE,"E14"),sQuery(id+"F0.wireOp",EDGE,"E15"),sQuery(id+"F0.wireOp",EDGE,"E16"),sQuery(id+"F0.wireOp",EDGE,"E17"),sQuery(id+"F0.wireOp",EDGE,"E18.filletArc"),sQuery(id+"F0.wireOp",EDGE,"E19.filletArc"),sQuery(id+"F0.wireOp",EDGE,"E20"),sQuery(id+"F0.wireOp",EDGE,"E21"),sQuery(id+"F0.wireOp",EDGE,"E22"),sQuery(id+"F0.wireOp",EDGE,"E23"),sQuery(id+"F0.wireOp",EDGE,"E24"),subQ2,subQ1])],"isStart":true})],"blendedInto":[makeQuery(id+"F1.opExtrude","CAP_FACE",FACE,{"disambiguationData":[OSD([sQuery(id+"F0.wireOp",EDGE,"E1"),sQuery(id+"F0.wireOp",EDGE,"E2"),sQuery(id+"F0.wireOp",EDGE,"E3"),sQuery(id+"F0.wireOp",EDGE,"E4"),sQuery(id+"F0.wireOp",EDGE,"E5"),sQuery(id+"F0.wireOp",EDGE,"E6"),sQuery(id+"F0.wireOp",EDGE,"E0.right"),subQ5,subQ4,subQ3,sQuery(id+"F0.wireOp",EDGE,"E10.filletArc"),sQuery(id+"F0.wireOp",EDGE,"E11.filletArc"),sQuery(id+"F0.wireOp",EDGE,"E12.filletArc"),sQuery(id+"F0.wireOp",EDGE,"E13.filletArc"),sQuery(id+"F0.wireOp",EDGE,"E14"),sQuery(id+"F0.wireOp",EDGE,"E15"),sQuery(id+"F0.wireOp",EDGE,"E16"),sQuery(id+"F0.wireOp",EDGE,"E17"),sQuery(id+"F0.wireOp",EDGE,"E18.filletArc"),sQuery(id+"F0.wireOp",EDGE,"E19.filletArc"),sQuery(id+"F0.wireOp",EDGE,"E20"),sQuery(id+"F0.wireOp",EDGE,"E21"),sQuery(id+"F0.wireOp",EDGE,"E22"),sQuery(id+"F0.wireOp",EDGE,"E23"),sQuery(id+"F0.wireOp",EDGE,"E24"),subQ2,subQ1])],"isStart":true})]})});var subQ7=makeQuery(id+"F15.imprint","INTERSECT",VERTEX,{"disambiguationData":[OD(0.0)],"derivedFrom":[subQ6,subQ0]});Q1=makeQuery(id+"F15.imprint","IMPRINT",FACE,{"disambiguationData":[TD([[makeQuery(id+"F15.imprint","IMPRINT",EDGE,{"disambiguationData":[TD([[subQ7,1.0]])],"derivedFrom":subQ0}),1.0]])]});}
            var Q2;
            {var subQ0=sQuery(id+"F15.wireOp",EDGE,"E71");var subQ1=sQuery(id+"F0.wireOp",EDGE,"E26");var subQ2=sQuery(id+"F0.wireOp",EDGE,"E25");var subQ3=sQuery(id+"F0.wireOp",EDGE,"E9.trimOffspring");var subQ4=sQuery(id+"F0.wireOp",EDGE,"E8.trimOffspring");var subQ5=sQuery(id+"F0.wireOp",EDGE,"E7");var subQ6=makeQuery(id+"F14.imprint","IMPRINT",EDGE,{"derivedFrom":makeQuery(id+"F2.opFillet","BLEND_EDGE",EDGE,{"blendedFrom":[makeQuery(id+"F1.opExtrude","CAP_EDGE",EDGE,{"disambiguationData":[OSD([subQ5,subQ4,subQ3,subQ2,subQ1])],"isStart":true}),makeQuery(id+"F1.opExtrude","CAP_FACE",FACE,{"disambiguationData":[OSD([sQuery(id+"F0.wireOp",EDGE,"E1"),sQuery(id+"F0.wireOp",EDGE,"E2"),sQuery(id+"F0.wireOp",EDGE,"E3"),sQuery(id+"F0.wireOp",EDGE,"E4"),sQuery(id+"F0.wireOp",EDGE,"E5"),sQuery(id+"F0.wireOp",EDGE,"E6"),sQuery(id+"F0.wireOp",EDGE,"E0.right"),subQ5,subQ4,subQ3,sQuery(id+"F0.wireOp",EDGE,"E10.filletArc"),sQuery(id+"F0.wireOp",EDGE,"E11.filletArc"),sQuery(id+"F0.wireOp",EDGE,"E12.filletArc"),sQuery(id+"F0.wireOp",EDGE,"E13.filletArc"),sQuery(id+"F0.wireOp",EDGE,"E14"),sQuery(id+"F0.wireOp",EDGE,"E15"),sQuery(id+"F0.wireOp",EDGE,"E16"),sQuery(id+"F0.wireOp",EDGE,"E17"),sQuery(id+"F0.wireOp",EDGE,"E18.filletArc"),sQuery(id+"F0.wireOp",EDGE,"E19.filletArc"),sQuery(id+"F0.wireOp",EDGE,"E20"),sQuery(id+"F0.wireOp",EDGE,"E21"),sQuery(id+"F0.wireOp",EDGE,"E22"),sQuery(id+"F0.wireOp",EDGE,"E23"),sQuery(id+"F0.wireOp",EDGE,"E24"),subQ2,subQ1])],"isStart":true})],"blendedInto":[makeQuery(id+"F1.opExtrude","CAP_FACE",FACE,{"disambiguationData":[OSD([sQuery(id+"F0.wireOp",EDGE,"E1"),sQuery(id+"F0.wireOp",EDGE,"E2"),sQuery(id+"F0.wireOp",EDGE,"E3"),sQuery(id+"F0.wireOp",EDGE,"E4"),sQuery(id+"F0.wireOp",EDGE,"E5"),sQuery(id+"F0.wireOp",EDGE,"E6"),sQuery(id+"F0.wireOp",EDGE,"E0.right"),subQ5,subQ4,subQ3,sQuery(id+"F0.wireOp",EDGE,"E10.filletArc"),sQuery(id+"F0.wireOp",EDGE,"E11.filletArc"),sQuery(id+"F0.wireOp",EDGE,"E12.filletArc"),sQuery(id+"F0.wireOp",EDGE,"E13.filletArc"),sQuery(id+"F0.wireOp",EDGE,"E14"),sQuery(id+"F0.wireOp",EDGE,"E15"),sQuery(id+"F0.wireOp",EDGE,"E16"),sQuery(id+"F0.wireOp",EDGE,"E17"),sQuery(id+"F0.wireOp",EDGE,"E18.filletArc"),sQuery(id+"F0.wireOp",EDGE,"E19.filletArc"),sQuery(id+"F0.wireOp",EDGE,"E20"),sQuery(id+"F0.wireOp",EDGE,"E21"),sQuery(id+"F0.wireOp",EDGE,"E22"),sQuery(id+"F0.wireOp",EDGE,"E23"),sQuery(id+"F0.wireOp",EDGE,"E24"),subQ2,subQ1])],"isStart":true})]})});var subQ7=makeQuery(id+"F15.imprint","INTERSECT",VERTEX,{"disambiguationData":[OD(0.0)],"derivedFrom":[subQ6,subQ0]});Q2=makeQuery(id+"F15.imprint","IMPRINT",FACE,{"disambiguationData":[TD([[makeQuery(id+"F15.imprint","IMPRINT",EDGE,{"disambiguationData":[TD([[subQ7,1.0]])],"derivedFrom":subQ0}),1.0]])]});}
            var Q3;
            {var subQ0=sQuery(id+"F15.wireOp",EDGE,"E71");var subQ1=sQuery(id+"F0.wireOp",EDGE,"E26");var subQ2=sQuery(id+"F0.wireOp",EDGE,"E25");var subQ3=sQuery(id+"F0.wireOp",EDGE,"E9.trimOffspring");var subQ4=sQuery(id+"F0.wireOp",EDGE,"E8.trimOffspring");var subQ5=sQuery(id+"F0.wireOp",EDGE,"E7");var subQ6=makeQuery(id+"F14.imprint","IMPRINT",EDGE,{"derivedFrom":makeQuery(id+"F2.opFillet","BLEND_EDGE",EDGE,{"blendedFrom":[makeQuery(id+"F1.opExtrude","CAP_EDGE",EDGE,{"disambiguationData":[OSD([subQ5,subQ4,subQ3,subQ2,subQ1])],"isStart":true}),makeQuery(id+"F1.opExtrude","CAP_FACE",FACE,{"disambiguationData":[OSD([sQuery(id+"F0.wireOp",EDGE,"E1"),sQuery(id+"F0.wireOp",EDGE,"E2"),sQuery(id+"F0.wireOp",EDGE,"E3"),sQuery(id+"F0.wireOp",EDGE,"E4"),sQuery(id+"F0.wireOp",EDGE,"E5"),sQuery(id+"F0.wireOp",EDGE,"E6"),sQuery(id+"F0.wireOp",EDGE,"E0.right"),subQ5,subQ4,subQ3,sQuery(id+"F0.wireOp",EDGE,"E10.filletArc"),sQuery(id+"F0.wireOp",EDGE,"E11.filletArc"),sQuery(id+"F0.wireOp",EDGE,"E12.filletArc"),sQuery(id+"F0.wireOp",EDGE,"E13.filletArc"),sQuery(id+"F0.wireOp",EDGE,"E14"),sQuery(id+"F0.wireOp",EDGE,"E15"),sQuery(id+"F0.wireOp",EDGE,"E16"),sQuery(id+"F0.wireOp",EDGE,"E17"),sQuery(id+"F0.wireOp",EDGE,"E18.filletArc"),sQuery(id+"F0.wireOp",EDGE,"E19.filletArc"),sQuery(id+"F0.wireOp",EDGE,"E20"),sQuery(id+"F0.wireOp",EDGE,"E21"),sQuery(id+"F0.wireOp",EDGE,"E22"),sQuery(id+"F0.wireOp",EDGE,"E23"),sQuery(id+"F0.wireOp",EDGE,"E24"),subQ2,subQ1])],"isStart":true})],"blendedInto":[makeQuery(id+"F1.opExtrude","CAP_FACE",FACE,{"disambiguationData":[OSD([sQuery(id+"F0.wireOp",EDGE,"E1"),sQuery(id+"F0.wireOp",EDGE,"E2"),sQuery(id+"F0.wireOp",EDGE,"E3"),sQuery(id+"F0.wireOp",EDGE,"E4"),sQuery(id+"F0.wireOp",EDGE,"E5"),sQuery(id+"F0.wireOp",EDGE,"E6"),sQuery(id+"F0.wireOp",EDGE,"E0.right"),subQ5,subQ4,subQ3,sQuery(id+"F0.wireOp",EDGE,"E10.filletArc"),sQuery(id+"F0.wireOp",EDGE,"E11.filletArc"),sQuery(id+"F0.wireOp",EDGE,"E12.filletArc"),sQuery(id+"F0.wireOp",EDGE,"E13.filletArc"),sQuery(id+"F0.wireOp",EDGE,"E14"),sQuery(id+"F0.wireOp",EDGE,"E15"),sQuery(id+"F0.wireOp",EDGE,"E16"),sQuery(id+"F0.wireOp",EDGE,"E17"),sQuery(id+"F0.wireOp",EDGE,"E18.filletArc"),sQuery(id+"F0.wireOp",EDGE,"E19.filletArc"),sQuery(id+"F0.wireOp",EDGE,"E20"),sQuery(id+"F0.wireOp",EDGE,"E21"),sQuery(id+"F0.wireOp",EDGE,"E22"),sQuery(id+"F0.wireOp",EDGE,"E23"),sQuery(id+"F0.wireOp",EDGE,"E24"),subQ2,subQ1])],"isStart":true})]})});var subQ7=makeQuery(id+"F15.imprint","INTERSECT",VERTEX,{"disambiguationData":[OD(0.0)],"derivedFrom":[subQ6,subQ0]});Q3=makeQuery(id+"F15.imprint","IMPRINT",FACE,{"disambiguationData":[TD([[makeQuery(id+"F15.imprint","IMPRINT",EDGE,{"disambiguationData":[TD([[subQ7,-1.0]])],"derivedFrom":subQ0}),1.0]])]});}
            extrude(context, id + "F16", {"entities" : qUnion([Q0, Q1, Q2, Q3]), "operationType" : NewBodyOperationType.ADD, "endBound" : BoundingType.SYMMETRIC, "depth" : 10 * mm});
        }
        {
            var Q0;
            {var subQ0=sQuery(id+"F12.wireOp",EDGE,"E58");var subQ1=sQuery(id+"F0.wireOp",EDGE,"E26");var subQ2=sQuery(id+"F0.wireOp",EDGE,"E25");var subQ3=sQuery(id+"F0.wireOp",EDGE,"E9.trimOffspring");var subQ4=sQuery(id+"F0.wireOp",EDGE,"E8.trimOffspring");var subQ5=sQuery(id+"F0.wireOp",EDGE,"E7");var subQ6=makeQuery(id+"F2.opFillet","BLEND_EDGE",EDGE,{"blendedFrom":[makeQuery(id+"F1.opExtrude","CAP_EDGE",EDGE,{"disambiguationData":[OSD([subQ5,subQ4,subQ3,subQ2,subQ1])],"isStart":false}),makeQuery(id+"F1.opExtrude","CAP_FACE",FACE,{"disambiguationData":[OSD([sQuery(id+"F0.wireOp",EDGE,"E1"),sQuery(id+"F0.wireOp",EDGE,"E2"),sQuery(id+"F0.wireOp",EDGE,"E3"),sQuery(id+"F0.wireOp",EDGE,"E4"),sQuery(id+"F0.wireOp",EDGE,"E5"),sQuery(id+"F0.wireOp",EDGE,"E6"),sQuery(id+"F0.wireOp",EDGE,"E0.right"),subQ5,subQ4,subQ3,sQuery(id+"F0.wireOp",EDGE,"E10.filletArc"),sQuery(id+"F0.wireOp",EDGE,"E11.filletArc"),sQuery(id+"F0.wireOp",EDGE,"E12.filletArc"),sQuery(id+"F0.wireOp",EDGE,"E13.filletArc"),sQuery(id+"F0.wireOp",EDGE,"E14"),sQuery(id+"F0.wireOp",EDGE,"E15"),sQuery(id+"F0.wireOp",EDGE,"E16"),sQuery(id+"F0.wireOp",EDGE,"E17"),sQuery(id+"F0.wireOp",EDGE,"E18.filletArc"),sQuery(id+"F0.wireOp",EDGE,"E19.filletArc"),sQuery(id+"F0.wireOp",EDGE,"E20"),sQuery(id+"F0.wireOp",EDGE,"E21"),sQuery(id+"F0.wireOp",EDGE,"E22"),sQuery(id+"F0.wireOp",EDGE,"E23"),sQuery(id+"F0.wireOp",EDGE,"E24"),subQ2,subQ1])],"isStart":false})],"blendedInto":[makeQuery(id+"F1.opExtrude","CAP_FACE",FACE,{"disambiguationData":[OSD([sQuery(id+"F0.wireOp",EDGE,"E1"),sQuery(id+"F0.wireOp",EDGE,"E2"),sQuery(id+"F0.wireOp",EDGE,"E3"),sQuery(id+"F0.wireOp",EDGE,"E4"),sQuery(id+"F0.wireOp",EDGE,"E5"),sQuery(id+"F0.wireOp",EDGE,"E6"),sQuery(id+"F0.wireOp",EDGE,"E0.right"),subQ5,subQ4,subQ3,sQuery(id+"F0.wireOp",EDGE,"E10.filletArc"),sQuery(id+"F0.wireOp",EDGE,"E11.filletArc"),sQuery(id+"F0.wireOp",EDGE,"E12.filletArc"),sQuery(id+"F0.wireOp",EDGE,"E13.filletArc"),sQuery(id+"F0.wireOp",EDGE,"E14"),sQuery(id+"F0.wireOp",EDGE,"E15"),sQuery(id+"F0.wireOp",EDGE,"E16"),sQuery(id+"F0.wireOp",EDGE,"E17"),sQuery(id+"F0.wireOp",EDGE,"E18.filletArc"),sQuery(id+"F0.wireOp",EDGE,"E19.filletArc"),sQuery(id+"F0.wireOp",EDGE,"E20"),sQuery(id+"F0.wireOp",EDGE,"E21"),sQuery(id+"F0.wireOp",EDGE,"E22"),sQuery(id+"F0.wireOp",EDGE,"E23"),sQuery(id+"F0.wireOp",EDGE,"E24"),subQ2,subQ1])],"isStart":false})]});var subQ7=makeQuery(id+"F12.imprint","INTERSECT",VERTEX,{"disambiguationData":[OD(0.0)],"derivedFrom":[subQ6,subQ0]});Q0=makeQuery(id+"F12.imprint","IMPRINT",FACE,{"disambiguationData":[TD([[makeQuery(id+"F12.imprint","IMPRINT",EDGE,{"disambiguationData":[TD([[subQ7,1.0]])],"derivedFrom":subQ0}),1.0]])]});}
            var Q1;
            {var subQ0=sQuery(id+"F12.wireOp",EDGE,"E58");var subQ1=sQuery(id+"F0.wireOp",EDGE,"E26");var subQ2=sQuery(id+"F0.wireOp",EDGE,"E25");var subQ3=sQuery(id+"F0.wireOp",EDGE,"E9.trimOffspring");var subQ4=sQuery(id+"F0.wireOp",EDGE,"E8.trimOffspring");var subQ5=sQuery(id+"F0.wireOp",EDGE,"E7");var subQ6=makeQuery(id+"F2.opFillet","BLEND_EDGE",EDGE,{"blendedFrom":[makeQuery(id+"F1.opExtrude","CAP_EDGE",EDGE,{"disambiguationData":[OSD([subQ5,subQ4,subQ3,subQ2,subQ1])],"isStart":false}),makeQuery(id+"F1.opExtrude","CAP_FACE",FACE,{"disambiguationData":[OSD([sQuery(id+"F0.wireOp",EDGE,"E1"),sQuery(id+"F0.wireOp",EDGE,"E2"),sQuery(id+"F0.wireOp",EDGE,"E3"),sQuery(id+"F0.wireOp",EDGE,"E4"),sQuery(id+"F0.wireOp",EDGE,"E5"),sQuery(id+"F0.wireOp",EDGE,"E6"),sQuery(id+"F0.wireOp",EDGE,"E0.right"),subQ5,subQ4,subQ3,sQuery(id+"F0.wireOp",EDGE,"E10.filletArc"),sQuery(id+"F0.wireOp",EDGE,"E11.filletArc"),sQuery(id+"F0.wireOp",EDGE,"E12.filletArc"),sQuery(id+"F0.wireOp",EDGE,"E13.filletArc"),sQuery(id+"F0.wireOp",EDGE,"E14"),sQuery(id+"F0.wireOp",EDGE,"E15"),sQuery(id+"F0.wireOp",EDGE,"E16"),sQuery(id+"F0.wireOp",EDGE,"E17"),sQuery(id+"F0.wireOp",EDGE,"E18.filletArc"),sQuery(id+"F0.wireOp",EDGE,"E19.filletArc"),sQuery(id+"F0.wireOp",EDGE,"E20"),sQuery(id+"F0.wireOp",EDGE,"E21"),sQuery(id+"F0.wireOp",EDGE,"E22"),sQuery(id+"F0.wireOp",EDGE,"E23"),sQuery(id+"F0.wireOp",EDGE,"E24"),subQ2,subQ1])],"isStart":false})],"blendedInto":[makeQuery(id+"F1.opExtrude","CAP_FACE",FACE,{"disambiguationData":[OSD([sQuery(id+"F0.wireOp",EDGE,"E1"),sQuery(id+"F0.wireOp",EDGE,"E2"),sQuery(id+"F0.wireOp",EDGE,"E3"),sQuery(id+"F0.wireOp",EDGE,"E4"),sQuery(id+"F0.wireOp",EDGE,"E5"),sQuery(id+"F0.wireOp",EDGE,"E6"),sQuery(id+"F0.wireOp",EDGE,"E0.right"),subQ5,subQ4,subQ3,sQuery(id+"F0.wireOp",EDGE,"E10.filletArc"),sQuery(id+"F0.wireOp",EDGE,"E11.filletArc"),sQuery(id+"F0.wireOp",EDGE,"E12.filletArc"),sQuery(id+"F0.wireOp",EDGE,"E13.filletArc"),sQuery(id+"F0.wireOp",EDGE,"E14"),sQuery(id+"F0.wireOp",EDGE,"E15"),sQuery(id+"F0.wireOp",EDGE,"E16"),sQuery(id+"F0.wireOp",EDGE,"E17"),sQuery(id+"F0.wireOp",EDGE,"E18.filletArc"),sQuery(id+"F0.wireOp",EDGE,"E19.filletArc"),sQuery(id+"F0.wireOp",EDGE,"E20"),sQuery(id+"F0.wireOp",EDGE,"E21"),sQuery(id+"F0.wireOp",EDGE,"E22"),sQuery(id+"F0.wireOp",EDGE,"E23"),sQuery(id+"F0.wireOp",EDGE,"E24"),subQ2,subQ1])],"isStart":false})]});var subQ7=makeQuery(id+"F12.imprint","INTERSECT",VERTEX,{"disambiguationData":[OD(0.0)],"derivedFrom":[subQ6,subQ0]});Q1=makeQuery(id+"F12.imprint","IMPRINT",FACE,{"disambiguationData":[TD([[makeQuery(id+"F12.imprint","IMPRINT",EDGE,{"disambiguationData":[TD([[subQ7,-1.0]])],"derivedFrom":subQ0}),1.0]])]});}
            var Q2;
            {var subQ0=sQuery(id+"F12.wireOp",EDGE,"E59");var subQ1=sQuery(id+"F0.wireOp",EDGE,"E26");var subQ2=sQuery(id+"F0.wireOp",EDGE,"E25");var subQ3=sQuery(id+"F0.wireOp",EDGE,"E9.trimOffspring");var subQ4=sQuery(id+"F0.wireOp",EDGE,"E8.trimOffspring");var subQ5=sQuery(id+"F0.wireOp",EDGE,"E7");var subQ6=makeQuery(id+"F2.opFillet","BLEND_EDGE",EDGE,{"blendedFrom":[makeQuery(id+"F1.opExtrude","CAP_EDGE",EDGE,{"disambiguationData":[OSD([subQ5,subQ4,subQ3,subQ2,subQ1])],"isStart":false}),makeQuery(id+"F1.opExtrude","CAP_FACE",FACE,{"disambiguationData":[OSD([sQuery(id+"F0.wireOp",EDGE,"E1"),sQuery(id+"F0.wireOp",EDGE,"E2"),sQuery(id+"F0.wireOp",EDGE,"E3"),sQuery(id+"F0.wireOp",EDGE,"E4"),sQuery(id+"F0.wireOp",EDGE,"E5"),sQuery(id+"F0.wireOp",EDGE,"E6"),sQuery(id+"F0.wireOp",EDGE,"E0.right"),subQ5,subQ4,subQ3,sQuery(id+"F0.wireOp",EDGE,"E10.filletArc"),sQuery(id+"F0.wireOp",EDGE,"E11.filletArc"),sQuery(id+"F0.wireOp",EDGE,"E12.filletArc"),sQuery(id+"F0.wireOp",EDGE,"E13.filletArc"),sQuery(id+"F0.wireOp",EDGE,"E14"),sQuery(id+"F0.wireOp",EDGE,"E15"),sQuery(id+"F0.wireOp",EDGE,"E16"),sQuery(id+"F0.wireOp",EDGE,"E17"),sQuery(id+"F0.wireOp",EDGE,"E18.filletArc"),sQuery(id+"F0.wireOp",EDGE,"E19.filletArc"),sQuery(id+"F0.wireOp",EDGE,"E20"),sQuery(id+"F0.wireOp",EDGE,"E21"),sQuery(id+"F0.wireOp",EDGE,"E22"),sQuery(id+"F0.wireOp",EDGE,"E23"),sQuery(id+"F0.wireOp",EDGE,"E24"),subQ2,subQ1])],"isStart":false})],"blendedInto":[makeQuery(id+"F1.opExtrude","CAP_FACE",FACE,{"disambiguationData":[OSD([sQuery(id+"F0.wireOp",EDGE,"E1"),sQuery(id+"F0.wireOp",EDGE,"E2"),sQuery(id+"F0.wireOp",EDGE,"E3"),sQuery(id+"F0.wireOp",EDGE,"E4"),sQuery(id+"F0.wireOp",EDGE,"E5"),sQuery(id+"F0.wireOp",EDGE,"E6"),sQuery(id+"F0.wireOp",EDGE,"E0.right"),subQ5,subQ4,subQ3,sQuery(id+"F0.wireOp",EDGE,"E10.filletArc"),sQuery(id+"F0.wireOp",EDGE,"E11.filletArc"),sQuery(id+"F0.wireOp",EDGE,"E12.filletArc"),sQuery(id+"F0.wireOp",EDGE,"E13.filletArc"),sQuery(id+"F0.wireOp",EDGE,"E14"),sQuery(id+"F0.wireOp",EDGE,"E15"),sQuery(id+"F0.wireOp",EDGE,"E16"),sQuery(id+"F0.wireOp",EDGE,"E17"),sQuery(id+"F0.wireOp",EDGE,"E18.filletArc"),sQuery(id+"F0.wireOp",EDGE,"E19.filletArc"),sQuery(id+"F0.wireOp",EDGE,"E20"),sQuery(id+"F0.wireOp",EDGE,"E21"),sQuery(id+"F0.wireOp",EDGE,"E22"),sQuery(id+"F0.wireOp",EDGE,"E23"),sQuery(id+"F0.wireOp",EDGE,"E24"),subQ2,subQ1])],"isStart":false})]});var subQ7=makeQuery(id+"F12.imprint","INTERSECT",VERTEX,{"disambiguationData":[OD(0.0)],"derivedFrom":[subQ6,subQ0]});Q2=makeQuery(id+"F12.imprint","IMPRINT",FACE,{"disambiguationData":[TD([[makeQuery(id+"F12.imprint","IMPRINT",EDGE,{"disambiguationData":[TD([[subQ7,-1.0]])],"derivedFrom":subQ0}),1.0]])]});}
            var Q3;
            {var subQ0=sQuery(id+"F12.wireOp",EDGE,"E59");var subQ1=sQuery(id+"F0.wireOp",EDGE,"E26");var subQ2=sQuery(id+"F0.wireOp",EDGE,"E25");var subQ3=sQuery(id+"F0.wireOp",EDGE,"E9.trimOffspring");var subQ4=sQuery(id+"F0.wireOp",EDGE,"E8.trimOffspring");var subQ5=sQuery(id+"F0.wireOp",EDGE,"E7");var subQ6=makeQuery(id+"F2.opFillet","BLEND_EDGE",EDGE,{"blendedFrom":[makeQuery(id+"F1.opExtrude","CAP_EDGE",EDGE,{"disambiguationData":[OSD([subQ5,subQ4,subQ3,subQ2,subQ1])],"isStart":false}),makeQuery(id+"F1.opExtrude","CAP_FACE",FACE,{"disambiguationData":[OSD([sQuery(id+"F0.wireOp",EDGE,"E1"),sQuery(id+"F0.wireOp",EDGE,"E2"),sQuery(id+"F0.wireOp",EDGE,"E3"),sQuery(id+"F0.wireOp",EDGE,"E4"),sQuery(id+"F0.wireOp",EDGE,"E5"),sQuery(id+"F0.wireOp",EDGE,"E6"),sQuery(id+"F0.wireOp",EDGE,"E0.right"),subQ5,subQ4,subQ3,sQuery(id+"F0.wireOp",EDGE,"E10.filletArc"),sQuery(id+"F0.wireOp",EDGE,"E11.filletArc"),sQuery(id+"F0.wireOp",EDGE,"E12.filletArc"),sQuery(id+"F0.wireOp",EDGE,"E13.filletArc"),sQuery(id+"F0.wireOp",EDGE,"E14"),sQuery(id+"F0.wireOp",EDGE,"E15"),sQuery(id+"F0.wireOp",EDGE,"E16"),sQuery(id+"F0.wireOp",EDGE,"E17"),sQuery(id+"F0.wireOp",EDGE,"E18.filletArc"),sQuery(id+"F0.wireOp",EDGE,"E19.filletArc"),sQuery(id+"F0.wireOp",EDGE,"E20"),sQuery(id+"F0.wireOp",EDGE,"E21"),sQuery(id+"F0.wireOp",EDGE,"E22"),sQuery(id+"F0.wireOp",EDGE,"E23"),sQuery(id+"F0.wireOp",EDGE,"E24"),subQ2,subQ1])],"isStart":false})],"blendedInto":[makeQuery(id+"F1.opExtrude","CAP_FACE",FACE,{"disambiguationData":[OSD([sQuery(id+"F0.wireOp",EDGE,"E1"),sQuery(id+"F0.wireOp",EDGE,"E2"),sQuery(id+"F0.wireOp",EDGE,"E3"),sQuery(id+"F0.wireOp",EDGE,"E4"),sQuery(id+"F0.wireOp",EDGE,"E5"),sQuery(id+"F0.wireOp",EDGE,"E6"),sQuery(id+"F0.wireOp",EDGE,"E0.right"),subQ5,subQ4,subQ3,sQuery(id+"F0.wireOp",EDGE,"E10.filletArc"),sQuery(id+"F0.wireOp",EDGE,"E11.filletArc"),sQuery(id+"F0.wireOp",EDGE,"E12.filletArc"),sQuery(id+"F0.wireOp",EDGE,"E13.filletArc"),sQuery(id+"F0.wireOp",EDGE,"E14"),sQuery(id+"F0.wireOp",EDGE,"E15"),sQuery(id+"F0.wireOp",EDGE,"E16"),sQuery(id+"F0.wireOp",EDGE,"E17"),sQuery(id+"F0.wireOp",EDGE,"E18.filletArc"),sQuery(id+"F0.wireOp",EDGE,"E19.filletArc"),sQuery(id+"F0.wireOp",EDGE,"E20"),sQuery(id+"F0.wireOp",EDGE,"E21"),sQuery(id+"F0.wireOp",EDGE,"E22"),sQuery(id+"F0.wireOp",EDGE,"E23"),sQuery(id+"F0.wireOp",EDGE,"E24"),subQ2,subQ1])],"isStart":false})]});var subQ7=makeQuery(id+"F12.imprint","INTERSECT",VERTEX,{"disambiguationData":[OD(0.0)],"derivedFrom":[subQ6,subQ0]});Q3=makeQuery(id+"F12.imprint","IMPRINT",FACE,{"disambiguationData":[TD([[makeQuery(id+"F12.imprint","IMPRINT",EDGE,{"disambiguationData":[TD([[subQ7,1.0]])],"derivedFrom":subQ0}),1.0]])]});}
            extrude(context, id + "F17", {"entities" : qUnion([Q0, Q1, Q2, Q3]), "operationType" : NewBodyOperationType.ADD, "depth" : 3 * mm});
        }
        {
            var Q0;
            {var subQ0=sQuery(id+"F15.wireOp",EDGE,"E72");var subQ1=sQuery(id+"F0.wireOp",EDGE,"E26");var subQ2=sQuery(id+"F0.wireOp",EDGE,"E25");var subQ3=sQuery(id+"F0.wireOp",EDGE,"E9.trimOffspring");var subQ4=sQuery(id+"F0.wireOp",EDGE,"E8.trimOffspring");var subQ5=sQuery(id+"F0.wireOp",EDGE,"E7");var subQ6=makeQuery(id+"F14.imprint","IMPRINT",EDGE,{"derivedFrom":makeQuery(id+"F2.opFillet","BLEND_EDGE",EDGE,{"blendedFrom":[makeQuery(id+"F1.opExtrude","CAP_EDGE",EDGE,{"disambiguationData":[OSD([subQ5,subQ4,subQ3,subQ2,subQ1])],"isStart":true}),makeQuery(id+"F1.opExtrude","CAP_FACE",FACE,{"disambiguationData":[OSD([sQuery(id+"F0.wireOp",EDGE,"E1"),sQuery(id+"F0.wireOp",EDGE,"E2"),sQuery(id+"F0.wireOp",EDGE,"E3"),sQuery(id+"F0.wireOp",EDGE,"E4"),sQuery(id+"F0.wireOp",EDGE,"E5"),sQuery(id+"F0.wireOp",EDGE,"E6"),sQuery(id+"F0.wireOp",EDGE,"E0.right"),subQ5,subQ4,subQ3,sQuery(id+"F0.wireOp",EDGE,"E10.filletArc"),sQuery(id+"F0.wireOp",EDGE,"E11.filletArc"),sQuery(id+"F0.wireOp",EDGE,"E12.filletArc"),sQuery(id+"F0.wireOp",EDGE,"E13.filletArc"),sQuery(id+"F0.wireOp",EDGE,"E14"),sQuery(id+"F0.wireOp",EDGE,"E15"),sQuery(id+"F0.wireOp",EDGE,"E16"),sQuery(id+"F0.wireOp",EDGE,"E17"),sQuery(id+"F0.wireOp",EDGE,"E18.filletArc"),sQuery(id+"F0.wireOp",EDGE,"E19.filletArc"),sQuery(id+"F0.wireOp",EDGE,"E20"),sQuery(id+"F0.wireOp",EDGE,"E21"),sQuery(id+"F0.wireOp",EDGE,"E22"),sQuery(id+"F0.wireOp",EDGE,"E23"),sQuery(id+"F0.wireOp",EDGE,"E24"),subQ2,subQ1])],"isStart":true})],"blendedInto":[makeQuery(id+"F1.opExtrude","CAP_FACE",FACE,{"disambiguationData":[OSD([sQuery(id+"F0.wireOp",EDGE,"E1"),sQuery(id+"F0.wireOp",EDGE,"E2"),sQuery(id+"F0.wireOp",EDGE,"E3"),sQuery(id+"F0.wireOp",EDGE,"E4"),sQuery(id+"F0.wireOp",EDGE,"E5"),sQuery(id+"F0.wireOp",EDGE,"E6"),sQuery(id+"F0.wireOp",EDGE,"E0.right"),subQ5,subQ4,subQ3,sQuery(id+"F0.wireOp",EDGE,"E10.filletArc"),sQuery(id+"F0.wireOp",EDGE,"E11.filletArc"),sQuery(id+"F0.wireOp",EDGE,"E12.filletArc"),sQuery(id+"F0.wireOp",EDGE,"E13.filletArc"),sQuery(id+"F0.wireOp",EDGE,"E14"),sQuery(id+"F0.wireOp",EDGE,"E15"),sQuery(id+"F0.wireOp",EDGE,"E16"),sQuery(id+"F0.wireOp",EDGE,"E17"),sQuery(id+"F0.wireOp",EDGE,"E18.filletArc"),sQuery(id+"F0.wireOp",EDGE,"E19.filletArc"),sQuery(id+"F0.wireOp",EDGE,"E20"),sQuery(id+"F0.wireOp",EDGE,"E21"),sQuery(id+"F0.wireOp",EDGE,"E22"),sQuery(id+"F0.wireOp",EDGE,"E23"),sQuery(id+"F0.wireOp",EDGE,"E24"),subQ2,subQ1])],"isStart":true})]})});var subQ7=makeQuery(id+"F15.imprint","INTERSECT",VERTEX,{"disambiguationData":[OD(0.0)],"derivedFrom":[subQ6,subQ0]});Q0=makeQuery(id+"F15.imprint","IMPRINT",FACE,{"disambiguationData":[TD([[makeQuery(id+"F15.imprint","IMPRINT",EDGE,{"disambiguationData":[TD([[subQ7,-1.0]])],"derivedFrom":subQ0}),1.0]])]});}
            var Q1;
            {var subQ0=sQuery(id+"F15.wireOp",EDGE,"E72");var subQ1=sQuery(id+"F0.wireOp",EDGE,"E26");var subQ2=sQuery(id+"F0.wireOp",EDGE,"E25");var subQ3=sQuery(id+"F0.wireOp",EDGE,"E9.trimOffspring");var subQ4=sQuery(id+"F0.wireOp",EDGE,"E8.trimOffspring");var subQ5=sQuery(id+"F0.wireOp",EDGE,"E7");var subQ6=makeQuery(id+"F14.imprint","IMPRINT",EDGE,{"derivedFrom":makeQuery(id+"F2.opFillet","BLEND_EDGE",EDGE,{"blendedFrom":[makeQuery(id+"F1.opExtrude","CAP_EDGE",EDGE,{"disambiguationData":[OSD([subQ5,subQ4,subQ3,subQ2,subQ1])],"isStart":true}),makeQuery(id+"F1.opExtrude","CAP_FACE",FACE,{"disambiguationData":[OSD([sQuery(id+"F0.wireOp",EDGE,"E1"),sQuery(id+"F0.wireOp",EDGE,"E2"),sQuery(id+"F0.wireOp",EDGE,"E3"),sQuery(id+"F0.wireOp",EDGE,"E4"),sQuery(id+"F0.wireOp",EDGE,"E5"),sQuery(id+"F0.wireOp",EDGE,"E6"),sQuery(id+"F0.wireOp",EDGE,"E0.right"),subQ5,subQ4,subQ3,sQuery(id+"F0.wireOp",EDGE,"E10.filletArc"),sQuery(id+"F0.wireOp",EDGE,"E11.filletArc"),sQuery(id+"F0.wireOp",EDGE,"E12.filletArc"),sQuery(id+"F0.wireOp",EDGE,"E13.filletArc"),sQuery(id+"F0.wireOp",EDGE,"E14"),sQuery(id+"F0.wireOp",EDGE,"E15"),sQuery(id+"F0.wireOp",EDGE,"E16"),sQuery(id+"F0.wireOp",EDGE,"E17"),sQuery(id+"F0.wireOp",EDGE,"E18.filletArc"),sQuery(id+"F0.wireOp",EDGE,"E19.filletArc"),sQuery(id+"F0.wireOp",EDGE,"E20"),sQuery(id+"F0.wireOp",EDGE,"E21"),sQuery(id+"F0.wireOp",EDGE,"E22"),sQuery(id+"F0.wireOp",EDGE,"E23"),sQuery(id+"F0.wireOp",EDGE,"E24"),subQ2,subQ1])],"isStart":true})],"blendedInto":[makeQuery(id+"F1.opExtrude","CAP_FACE",FACE,{"disambiguationData":[OSD([sQuery(id+"F0.wireOp",EDGE,"E1"),sQuery(id+"F0.wireOp",EDGE,"E2"),sQuery(id+"F0.wireOp",EDGE,"E3"),sQuery(id+"F0.wireOp",EDGE,"E4"),sQuery(id+"F0.wireOp",EDGE,"E5"),sQuery(id+"F0.wireOp",EDGE,"E6"),sQuery(id+"F0.wireOp",EDGE,"E0.right"),subQ5,subQ4,subQ3,sQuery(id+"F0.wireOp",EDGE,"E10.filletArc"),sQuery(id+"F0.wireOp",EDGE,"E11.filletArc"),sQuery(id+"F0.wireOp",EDGE,"E12.filletArc"),sQuery(id+"F0.wireOp",EDGE,"E13.filletArc"),sQuery(id+"F0.wireOp",EDGE,"E14"),sQuery(id+"F0.wireOp",EDGE,"E15"),sQuery(id+"F0.wireOp",EDGE,"E16"),sQuery(id+"F0.wireOp",EDGE,"E17"),sQuery(id+"F0.wireOp",EDGE,"E18.filletArc"),sQuery(id+"F0.wireOp",EDGE,"E19.filletArc"),sQuery(id+"F0.wireOp",EDGE,"E20"),sQuery(id+"F0.wireOp",EDGE,"E21"),sQuery(id+"F0.wireOp",EDGE,"E22"),sQuery(id+"F0.wireOp",EDGE,"E23"),sQuery(id+"F0.wireOp",EDGE,"E24"),subQ2,subQ1])],"isStart":true})]})});var subQ7=makeQuery(id+"F15.imprint","INTERSECT",VERTEX,{"disambiguationData":[OD(0.0)],"derivedFrom":[subQ6,subQ0]});Q1=makeQuery(id+"F15.imprint","IMPRINT",FACE,{"disambiguationData":[TD([[makeQuery(id+"F15.imprint","IMPRINT",EDGE,{"disambiguationData":[TD([[subQ7,1.0]])],"derivedFrom":subQ0}),1.0]])]});}
            var Q2;
            {var subQ0=sQuery(id+"F15.wireOp",EDGE,"E73");var subQ1=sQuery(id+"F0.wireOp",EDGE,"E26");var subQ2=sQuery(id+"F0.wireOp",EDGE,"E25");var subQ3=sQuery(id+"F0.wireOp",EDGE,"E9.trimOffspring");var subQ4=sQuery(id+"F0.wireOp",EDGE,"E8.trimOffspring");var subQ5=sQuery(id+"F0.wireOp",EDGE,"E7");var subQ6=makeQuery(id+"F14.imprint","IMPRINT",EDGE,{"derivedFrom":makeQuery(id+"F2.opFillet","BLEND_EDGE",EDGE,{"blendedFrom":[makeQuery(id+"F1.opExtrude","CAP_EDGE",EDGE,{"disambiguationData":[OSD([subQ5,subQ4,subQ3,subQ2,subQ1])],"isStart":true}),makeQuery(id+"F1.opExtrude","CAP_FACE",FACE,{"disambiguationData":[OSD([sQuery(id+"F0.wireOp",EDGE,"E1"),sQuery(id+"F0.wireOp",EDGE,"E2"),sQuery(id+"F0.wireOp",EDGE,"E3"),sQuery(id+"F0.wireOp",EDGE,"E4"),sQuery(id+"F0.wireOp",EDGE,"E5"),sQuery(id+"F0.wireOp",EDGE,"E6"),sQuery(id+"F0.wireOp",EDGE,"E0.right"),subQ5,subQ4,subQ3,sQuery(id+"F0.wireOp",EDGE,"E10.filletArc"),sQuery(id+"F0.wireOp",EDGE,"E11.filletArc"),sQuery(id+"F0.wireOp",EDGE,"E12.filletArc"),sQuery(id+"F0.wireOp",EDGE,"E13.filletArc"),sQuery(id+"F0.wireOp",EDGE,"E14"),sQuery(id+"F0.wireOp",EDGE,"E15"),sQuery(id+"F0.wireOp",EDGE,"E16"),sQuery(id+"F0.wireOp",EDGE,"E17"),sQuery(id+"F0.wireOp",EDGE,"E18.filletArc"),sQuery(id+"F0.wireOp",EDGE,"E19.filletArc"),sQuery(id+"F0.wireOp",EDGE,"E20"),sQuery(id+"F0.wireOp",EDGE,"E21"),sQuery(id+"F0.wireOp",EDGE,"E22"),sQuery(id+"F0.wireOp",EDGE,"E23"),sQuery(id+"F0.wireOp",EDGE,"E24"),subQ2,subQ1])],"isStart":true})],"blendedInto":[makeQuery(id+"F1.opExtrude","CAP_FACE",FACE,{"disambiguationData":[OSD([sQuery(id+"F0.wireOp",EDGE,"E1"),sQuery(id+"F0.wireOp",EDGE,"E2"),sQuery(id+"F0.wireOp",EDGE,"E3"),sQuery(id+"F0.wireOp",EDGE,"E4"),sQuery(id+"F0.wireOp",EDGE,"E5"),sQuery(id+"F0.wireOp",EDGE,"E6"),sQuery(id+"F0.wireOp",EDGE,"E0.right"),subQ5,subQ4,subQ3,sQuery(id+"F0.wireOp",EDGE,"E10.filletArc"),sQuery(id+"F0.wireOp",EDGE,"E11.filletArc"),sQuery(id+"F0.wireOp",EDGE,"E12.filletArc"),sQuery(id+"F0.wireOp",EDGE,"E13.filletArc"),sQuery(id+"F0.wireOp",EDGE,"E14"),sQuery(id+"F0.wireOp",EDGE,"E15"),sQuery(id+"F0.wireOp",EDGE,"E16"),sQuery(id+"F0.wireOp",EDGE,"E17"),sQuery(id+"F0.wireOp",EDGE,"E18.filletArc"),sQuery(id+"F0.wireOp",EDGE,"E19.filletArc"),sQuery(id+"F0.wireOp",EDGE,"E20"),sQuery(id+"F0.wireOp",EDGE,"E21"),sQuery(id+"F0.wireOp",EDGE,"E22"),sQuery(id+"F0.wireOp",EDGE,"E23"),sQuery(id+"F0.wireOp",EDGE,"E24"),subQ2,subQ1])],"isStart":true})]})});var subQ7=makeQuery(id+"F15.imprint","INTERSECT",VERTEX,{"disambiguationData":[OD(0.0)],"derivedFrom":[subQ6,subQ0]});Q2=makeQuery(id+"F15.imprint","IMPRINT",FACE,{"disambiguationData":[TD([[makeQuery(id+"F15.imprint","IMPRINT",EDGE,{"disambiguationData":[TD([[subQ7,1.0]])],"derivedFrom":subQ0}),1.0]])]});}
            var Q3;
            {var subQ0=sQuery(id+"F15.wireOp",EDGE,"E73");var subQ1=sQuery(id+"F0.wireOp",EDGE,"E26");var subQ2=sQuery(id+"F0.wireOp",EDGE,"E25");var subQ3=sQuery(id+"F0.wireOp",EDGE,"E9.trimOffspring");var subQ4=sQuery(id+"F0.wireOp",EDGE,"E8.trimOffspring");var subQ5=sQuery(id+"F0.wireOp",EDGE,"E7");var subQ6=makeQuery(id+"F14.imprint","IMPRINT",EDGE,{"derivedFrom":makeQuery(id+"F2.opFillet","BLEND_EDGE",EDGE,{"blendedFrom":[makeQuery(id+"F1.opExtrude","CAP_EDGE",EDGE,{"disambiguationData":[OSD([subQ5,subQ4,subQ3,subQ2,subQ1])],"isStart":true}),makeQuery(id+"F1.opExtrude","CAP_FACE",FACE,{"disambiguationData":[OSD([sQuery(id+"F0.wireOp",EDGE,"E1"),sQuery(id+"F0.wireOp",EDGE,"E2"),sQuery(id+"F0.wireOp",EDGE,"E3"),sQuery(id+"F0.wireOp",EDGE,"E4"),sQuery(id+"F0.wireOp",EDGE,"E5"),sQuery(id+"F0.wireOp",EDGE,"E6"),sQuery(id+"F0.wireOp",EDGE,"E0.right"),subQ5,subQ4,subQ3,sQuery(id+"F0.wireOp",EDGE,"E10.filletArc"),sQuery(id+"F0.wireOp",EDGE,"E11.filletArc"),sQuery(id+"F0.wireOp",EDGE,"E12.filletArc"),sQuery(id+"F0.wireOp",EDGE,"E13.filletArc"),sQuery(id+"F0.wireOp",EDGE,"E14"),sQuery(id+"F0.wireOp",EDGE,"E15"),sQuery(id+"F0.wireOp",EDGE,"E16"),sQuery(id+"F0.wireOp",EDGE,"E17"),sQuery(id+"F0.wireOp",EDGE,"E18.filletArc"),sQuery(id+"F0.wireOp",EDGE,"E19.filletArc"),sQuery(id+"F0.wireOp",EDGE,"E20"),sQuery(id+"F0.wireOp",EDGE,"E21"),sQuery(id+"F0.wireOp",EDGE,"E22"),sQuery(id+"F0.wireOp",EDGE,"E23"),sQuery(id+"F0.wireOp",EDGE,"E24"),subQ2,subQ1])],"isStart":true})],"blendedInto":[makeQuery(id+"F1.opExtrude","CAP_FACE",FACE,{"disambiguationData":[OSD([sQuery(id+"F0.wireOp",EDGE,"E1"),sQuery(id+"F0.wireOp",EDGE,"E2"),sQuery(id+"F0.wireOp",EDGE,"E3"),sQuery(id+"F0.wireOp",EDGE,"E4"),sQuery(id+"F0.wireOp",EDGE,"E5"),sQuery(id+"F0.wireOp",EDGE,"E6"),sQuery(id+"F0.wireOp",EDGE,"E0.right"),subQ5,subQ4,subQ3,sQuery(id+"F0.wireOp",EDGE,"E10.filletArc"),sQuery(id+"F0.wireOp",EDGE,"E11.filletArc"),sQuery(id+"F0.wireOp",EDGE,"E12.filletArc"),sQuery(id+"F0.wireOp",EDGE,"E13.filletArc"),sQuery(id+"F0.wireOp",EDGE,"E14"),sQuery(id+"F0.wireOp",EDGE,"E15"),sQuery(id+"F0.wireOp",EDGE,"E16"),sQuery(id+"F0.wireOp",EDGE,"E17"),sQuery(id+"F0.wireOp",EDGE,"E18.filletArc"),sQuery(id+"F0.wireOp",EDGE,"E19.filletArc"),sQuery(id+"F0.wireOp",EDGE,"E20"),sQuery(id+"F0.wireOp",EDGE,"E21"),sQuery(id+"F0.wireOp",EDGE,"E22"),sQuery(id+"F0.wireOp",EDGE,"E23"),sQuery(id+"F0.wireOp",EDGE,"E24"),subQ2,subQ1])],"isStart":true})]})});var subQ7=makeQuery(id+"F15.imprint","INTERSECT",VERTEX,{"disambiguationData":[OD(0.0)],"derivedFrom":[subQ6,subQ0]});Q3=makeQuery(id+"F15.imprint","IMPRINT",FACE,{"disambiguationData":[TD([[makeQuery(id+"F15.imprint","IMPRINT",EDGE,{"disambiguationData":[TD([[subQ7,-1.0]])],"derivedFrom":subQ0}),1.0]])]});}
            extrude(context, id + "F18", {"entities" : qUnion([Q0, Q1, Q2, Q3]), "operationType" : NewBodyOperationType.ADD, "depth" : 3 * mm});
        }
        {
            var Q0;
            Q0=makeQuery(id+"F1.opExtrude","CAP_EDGE",EDGE,{"disambiguationData":[OSD([sQuery(id+"F0.wireOp",EDGE,"E2")])],"isStart":true});
            fillet(context, id + "F19", {"entities" : qUnion([Q0]), "radius" : 5 * mm, "tangentPropagation" : true, "allowEdgeOverflow" : false});
        }
        {
            var Q0;
            Q0=makeQuery(id+"F4.imprint","IMPRINT",FACE,{"disambiguationData":[TD([[makeQuery(id+"F4.imprint","IMPRINT",EDGE,{"derivedFrom":sQuery(id+"F4.wireOp",EDGE,"E27")}),1.0]])]});
            var Q1;
            Q1=makeQuery(id+"F4.imprint","IMPRINT",FACE,{"disambiguationData":[TD([[makeQuery(id+"F4.imprint","IMPRINT",EDGE,{"derivedFrom":sQuery(id+"F4.wireOp",EDGE,"E42.bottom")}),-1.0]])]});
            var Q2;
            Q2=makeQuery(id+"F4.imprint","IMPRINT",FACE,{"disambiguationData":[TD([[makeQuery(id+"F4.imprint","IMPRINT",EDGE,{"derivedFrom":sQuery(id+"F4.wireOp",EDGE,"E31")}),-1.0]])]});
            extrude(context, id + "F20", {"entities" : qUnion([Q0, Q1, Q2]), "operationType" : NewBodyOperationType.ADD, "depth" : 3 * mm});
        }
        {
            var Q0;
            Q0=makeQuery(id+"F4.imprint","IMPRINT",FACE,{"disambiguationData":[TD([[makeQuery(id+"F4.imprint","IMPRINT",EDGE,{"derivedFrom":sQuery(id+"F4.wireOp",EDGE,"E39")}),1.0]])]});
            var Q1;
            Q1=makeQuery(id+"F4.imprint","IMPRINT",FACE,{"disambiguationData":[TD([[makeQuery(id+"F4.imprint","IMPRINT",EDGE,{"derivedFrom":sQuery(id+"F4.wireOp",EDGE,"E40")}),1.0]])]});
            extrude(context, id + "F21", {"entities" : qUnion([Q0, Q1]), "operationType" : NewBodyOperationType.ADD, "depth" : 4 * mm});
        }
        {
            var Q0;
            Q0=makeQuery(id+"F1.opExtrude","SWEPT_FACE",FACE,{"disambiguationData":[OSD([sQuery(id+"F0.wireOp",EDGE,"E2")])]});
            var sketch = newSketch(context, id + "F22", { "sketchPlane" : qUnion([Q0])});
            skLineSegment(sketch, "E82", {"start": v(-26.72, 14.1) * mm, "end": v(-87.56, 14.1) * mm});
            skLineSegment(sketch, "E83", {"start": v(-87.56, 14.1) * mm, "end": v(-87.56, -13.43) * mm});
            skLineSegment(sketch, "E84", {"start": v(-87.56, -13.43) * mm, "end": v(-26.72, -13.43) * mm});
            skLineSegment(sketch, "E85", {"start": v(-26.72, -13.43) * mm, "end": v(-26.72, 14.1) * mm});
            skLineSegment(sketch, "E86", {"start": v(-41.65, 12.1) * mm, "end": v(-71.65, 12.1) * mm});
            skLineSegment(sketch, "E87", {"start": v(-71.65, 12.1) * mm, "end": v(-80.5, 0) * mm});
            skLineSegment(sketch, "E88", {"start": v(-80.5, 0) * mm, "end": v(-71.65, -12.1) * mm});
            skLineSegment(sketch, "E89", {"start": v(-71.65, -12.1) * mm, "end": v(-41.65, -12.1) * mm});
            skLineSegment(sketch, "E90", {"start": v(-41.65, -12.1) * mm, "end": v(-41.65, 12.1) * mm});
            skSolve(sketch);
        }
        {
            var Q0;
            Q0=makeQuery(id+"F22.imprint","IMPRINT",FACE,{"disambiguationData":[TD([[makeQuery(id+"F22.imprint","IMPRINT",EDGE,{"derivedFrom":sQuery(id+"F22.wireOp",EDGE,"E82")}),1.0]])]});
            extrude(context, id + "F23", {"entities" : qUnion([Q0]), "operationType" : NewBodyOperationType.ADD, "depth" : 5 * mm});
        }
        {
            var Q0;
            Q0=makeQuery(id+"F23.opExtrude","CAP_EDGE",EDGE,{"disambiguationData":[OSD([sQuery(id+"F22.wireOp",EDGE,"E84")])],"isStart":false});
            var Q1;
            Q1=makeQuery(id+"F23.opExtrude","CAP_EDGE",EDGE,{"disambiguationData":[OSD([sQuery(id+"F22.wireOp",EDGE,"E82")])],"isStart":false});
            var Q2;
            Q2=makeQuery(id+"F23.opExtrude","CAP_EDGE",EDGE,{"disambiguationData":[OSD([sQuery(id+"F22.wireOp",EDGE,"E83")])],"isStart":false});
            fillet(context, id + "F24", {"entities" : qUnion([Q0, Q1, Q2]), "radius" : 5 * mm, "tangentPropagation" : true, "allowEdgeOverflow" : false});
        }
        {
            var Q0;
            Q0=makeQuery(id+"F1.opExtrude","SWEPT_FACE",FACE,{"disambiguationData":[OSD([sQuery(id+"F0.wireOp",EDGE,"E4")])]});
            var sketch = newSketch(context, id + "F25", { "sketchPlane" : qUnion([Q0])});
            skLineSegment(sketch, "E91.bottom", {"start": v(34.65, 24.44) * mm, "end": v(19.65, 24.44) * mm});
            skLineSegment(sketch, "E91.top", {"start": v(34.65, -25.56) * mm, "end": v(19.65, -25.56) * mm});
            skLineSegment(sketch, "E91.left", {"start": v(39.65, 19.44) * mm, "end": v(39.65, -20.56) * mm});
            skLineSegment(sketch, "E91.right", {"start": v(14.65, 19.44) * mm, "end": v(14.65, -20.56) * mm});
            skPoint(sketch, "E92.visualSharp", {"position": v(39.65, -25.56) * mm});
            skArc(sketch, "E92.filletArc", {"start": v(34.65, -25.56) * mm, "mid": v(38.18, -24.1) * mm, "end": v(39.65, -20.56) * mm});
            skPoint(sketch, "E93.visualSharp", {"position": v(14.65, -25.56) * mm});
            skArc(sketch, "E93.filletArc", {"start": v(14.65, -20.56) * mm, "mid": v(16.11, -24.1) * mm, "end": v(19.65, -25.56) * mm});
            skPoint(sketch, "E94.visualSharp", {"position": v(14.65, 24.44) * mm});
            skArc(sketch, "E94.filletArc", {"start": v(19.65, 24.44) * mm, "mid": v(16.11, 22.97) * mm, "end": v(14.65, 19.44) * mm});
            skPoint(sketch, "E95.visualSharp", {"position": v(39.65, 24.44) * mm});
            skArc(sketch, "E95.filletArc", {"start": v(39.65, 19.44) * mm, "mid": v(38.18, 22.97) * mm, "end": v(34.65, 24.44) * mm});
            skSolve(sketch);
        }
        {
            var Q0;
            Q0=makeQuery(id+"F25.imprint","IMPRINT",FACE,{"disambiguationData":[TD([[makeQuery(id+"F25.imprint","IMPRINT",EDGE,{"derivedFrom":sQuery(id+"F25.wireOp",EDGE,"E91.bottom")}),1.0]])]});
            extrude(context, id + "F26", {"entities" : qUnion([Q0]), "operationType" : NewBodyOperationType.REMOVE, "oppositeDirection" : true, "depth" : 2 * mm});
        }
        {
            var Q0;
            Q0=makeQuery(id+"F1.opExtrude","SWEPT_FACE",FACE,{"disambiguationData":[OSD([sQuery(id+"F0.wireOp",EDGE,"E16")])]});
            var sketch = newSketch(context, id + "F27", { "sketchPlane" : qUnion([Q0])});
            skLineSegment(sketch, "E96.bottom", {"start": v(-43.07, 15.57) * mm, "end": v(40.76, 15.57) * mm});
            skLineSegment(sketch, "E96.top", {"start": v(-43.07, 9.29) * mm, "end": v(40.76, 9.29) * mm});
            skLineSegment(sketch, "E96.left", {"start": v(-43.07, 15.57) * mm, "end": v(-43.07, 9.29) * mm});
            skLineSegment(sketch, "E96.right", {"start": v(40.76, 15.57) * mm, "end": v(40.76, 9.29) * mm});
            skSolve(sketch);
        }
        {
            var Q0;
            Q0=makeQuery(id+"F27.imprint","IMPRINT",FACE,{"disambiguationData":[TD([[makeQuery(id+"F27.imprint","IMPRINT",EDGE,{"derivedFrom":sQuery(id+"F27.wireOp",EDGE,"E96.bottom")}),-1.0]])]});
            extrude(context, id + "F28", {"entities" : qUnion([Q0]), "operationType" : NewBodyOperationType.REMOVE, "oppositeDirection" : true, "depth" : 25 * mm});
        }
        {
            var Q0;
            Q0=makeQuery(id+"F1.opExtrude","SWEPT_FACE",FACE,{"disambiguationData":[OSD([sQuery(id+"F0.wireOp",EDGE,"E17")])]});
            var sketch = newSketch(context, id + "F29", { "sketchPlane" : qUnion([Q0])});
            skLineSegment(sketch, "E97.bottom", {"start": v(0.4, -39.42) * mm, "end": v(8.37, -39.42) * mm});
            skLineSegment(sketch, "E97.top", {"start": v(0.4, 40.4) * mm, "end": v(8.37, 40.4) * mm});
            skLineSegment(sketch, "E97.left", {"start": v(0.4, -39.42) * mm, "end": v(0.4, 40.4) * mm});
            skLineSegment(sketch, "E97.right", {"start": v(8.37, -39.42) * mm, "end": v(8.37, 40.4) * mm});
            skLineSegment(sketch, "E98.bottom", {"start": v(23.61, 29.03) * mm, "end": v(17.74, 29.03) * mm});
            skLineSegment(sketch, "E98.top", {"start": v(23.61, 0) * mm, "end": v(17.74, 0) * mm});
            skLineSegment(sketch, "E98.left", {"start": v(23.61, 29.03) * mm, "end": v(23.61, 0) * mm});
            skLineSegment(sketch, "E98.right", {"start": v(17.74, 29.03) * mm, "end": v(17.74, 0) * mm});
            skLineSegment(sketch, "E99.bottom", {"start": v(23.4, -11.96) * mm, "end": v(17.74, -11.96) * mm});
            skLineSegment(sketch, "E99.top", {"start": v(23.4, -35.08) * mm, "end": v(17.74, -35.08) * mm});
            skLineSegment(sketch, "E99.left", {"start": v(23.4, -11.96) * mm, "end": v(23.4, -35.08) * mm});
            skLineSegment(sketch, "E99.right", {"start": v(17.74, -11.96) * mm, "end": v(17.74, -35.08) * mm});
            skSolve(sketch);
        }
        {
            var Q0;
            Q0=sQuery(id+"F29.wireOp",EDGE,"E98.bottom");
            var Q1;
            Q1=sQuery(id+"F29.wireOp",EDGE,"E98.left");
            var Q2;
            Q2=sQuery(id+"F29.wireOp",EDGE,"E98.right");
            var Q3;
            Q3=sQuery(id+"F29.wireOp",EDGE,"E98.top");
            var Q4;
            Q4=sQuery(id+"F29.wireOp",EDGE,"E99.right");
            var Q5;
            Q5=sQuery(id+"F29.wireOp",EDGE,"E99.left");
            var Q6;
            Q6=sQuery(id+"F29.wireOp",EDGE,"E99.top");
            var Q7;
            Q7=sQuery(id+"F29.wireOp",EDGE,"E99.bottom");
            extrude(context, id + "F30", {"bodyType" : ToolBodyType.SURFACE, "surfaceEntities" : qUnion([Q0, Q1, Q2, Q3, Q4, Q5, Q6, Q7]), "depth" : 8 * mm});
        }
        {
            var Q0;
            Q0=makeQuery(id+"F12.imprint","IMPRINT",FACE,{"disambiguationData":[TD([[makeQuery(id+"F12.imprint","IMPRINT",EDGE,{"derivedFrom":sQuery(id+"F12.wireOp",EDGE,"E60")}),-1.0]])]});
            var Q1;
            Q1=makeQuery(id+"F12.imprint","IMPRINT",FACE,{"disambiguationData":[TD([[makeQuery(id+"F12.imprint","IMPRINT",EDGE,{"derivedFrom":sQuery(id+"F12.wireOp",EDGE,"E65")}),1.0]])]});
            extrude(context, id + "F31", {"entities" : qUnion([Q0, Q1]), "operationType" : NewBodyOperationType.ADD, "depth" : 1 * mm});
        }
        {
            var Q0;
            Q0=makeQuery(id+"F31.opExtrude","CAP_EDGE",EDGE,{"disambiguationData":[OSD([sQuery(id+"F12.wireOp",EDGE,"E60"),sQuery(id+"F12.wireOp",EDGE,"E64")])],"isStart":false});
            var Q1;
            Q1=makeQuery(id+"F31.opExtrude","CAP_EDGE",EDGE,{"disambiguationData":[OSD([sQuery(id+"F12.wireOp",EDGE,"E67")])],"isStart":false});
            fillet(context, id + "F32", {"entities" : qUnion([Q0, Q1]), "radius" : 5 * mm, "tangentPropagation" : true, "allowEdgeOverflow" : false});
        }
        {
            var Q0;
            Q0=makeQuery(id+"F31.opExtrude","CAP_EDGE",EDGE,{"disambiguationData":[OSD([sQuery(id+"F12.wireOp",EDGE,"E62")])],"isStart":false});
            var Q1;
            Q1=makeQuery(id+"F31.opExtrude","CAP_EDGE",EDGE,{"disambiguationData":[OSD([sQuery(id+"F12.wireOp",EDGE,"E65"),sQuery(id+"F12.wireOp",EDGE,"E69")])],"isStart":false});
            var Q2;
            Q2=makeQuery(id+"F31.opExtrude","CAP_EDGE",EDGE,{"disambiguationData":[OSD([sQuery(id+"F12.wireOp",EDGE,"E61")])],"isStart":false});
            var Q3;
            Q3=makeQuery(id+"F31.opExtrude","CAP_EDGE",EDGE,{"disambiguationData":[OSD([sQuery(id+"F12.wireOp",EDGE,"E66")])],"isStart":false});
            chamfer(context, id + "F33", {"entities" : qUnion([Q0, Q1, Q2, Q3]), "width" : 0.8 * mm, "tangentPropagation" : true});
        }
        {
            var Q0;
            Q0=makeQuery(id+"F15.imprint","IMPRINT",FACE,{"disambiguationData":[TD([[makeQuery(id+"F15.imprint","IMPRINT",EDGE,{"derivedFrom":sQuery(id+"F15.wireOp",EDGE,"E78")}),-1.0]])]});
            var Q1;
            {var subQ4=sQuery(id+"F15.wireOp",EDGE,"E74");Q1=makeQuery(id+"F15.imprint","IMPRINT",FACE,{"disambiguationData":[TD([[makeQuery(id+"F15.imprint","IMPRINT",EDGE,{"derivedFrom":subQ4}),1.0]])]});}
            extrude(context, id + "F34", {"entities" : qUnion([Q0, Q1]), "operationType" : NewBodyOperationType.ADD, "depth" : 1 * mm});
        }
        {
            var Q0;
            Q0=makeQuery(id+"F34.opExtrude","CAP_EDGE",EDGE,{"disambiguationData":[OSD([sQuery(id+"F15.wireOp",EDGE,"E80")])],"isStart":false});
            var Q1;
            Q1=makeQuery(id+"F34.opExtrude","CAP_EDGE",EDGE,{"disambiguationData":[OSD([sQuery(id+"F15.wireOp",EDGE,"E74")])],"isStart":false});
            fillet(context, id + "F35", {"entities" : qUnion([Q0, Q1]), "radius" : 5 * mm, "tangentPropagation" : true, "allowEdgeOverflow" : false});
        }
        {
            var Q0;
            Q0=makeQuery(id+"F34.opExtrude","CAP_EDGE",EDGE,{"disambiguationData":[OSD([sQuery(id+"F15.wireOp",EDGE,"E78")])],"isStart":false});
            var Q1;
            Q1=makeQuery(id+"F34.opExtrude","CAP_EDGE",EDGE,{"disambiguationData":[OSD([sQuery(id+"F15.wireOp",EDGE,"E76")])],"isStart":false});
            chamfer(context, id + "F36", {"entities" : qUnion([Q0, Q1]), "width" : .8 * mm, "tangentPropagation" : true});
        }
        {
            var Q0;
            Q0=makeQuery(id+"F1.opExtrude","SWEPT_FACE",FACE,{"disambiguationData":[OSD([sQuery(id+"F0.wireOp",EDGE,"E0.right")])]});
            var sketch = newSketch(context, id + "F37", { "sketchPlane" : qUnion([Q0])});
            skCircle(sketch, "E100", {"center": v(-27.9, -28.35) * mm, "radius": 1.92 * mm});
            skCircle(sketch, "E101", {"center": v(-27.9, -28.35) * mm, "radius": 1.05 * mm});
            skSolve(sketch);
        }
        {
            var Q0;
            Q0=makeQuery(id+"F37.imprint","IMPRINT",FACE,{"disambiguationData":[TD([[makeQuery(id+"F37.imprint","IMPRINT",EDGE,{"derivedFrom":sQuery(id+"F37.wireOp",EDGE,"E100")}),1.0]])]});
            extrude(context, id + "F38", {"entities" : qUnion([Q0]), "depth" : 5 * mm});
        }
    });
